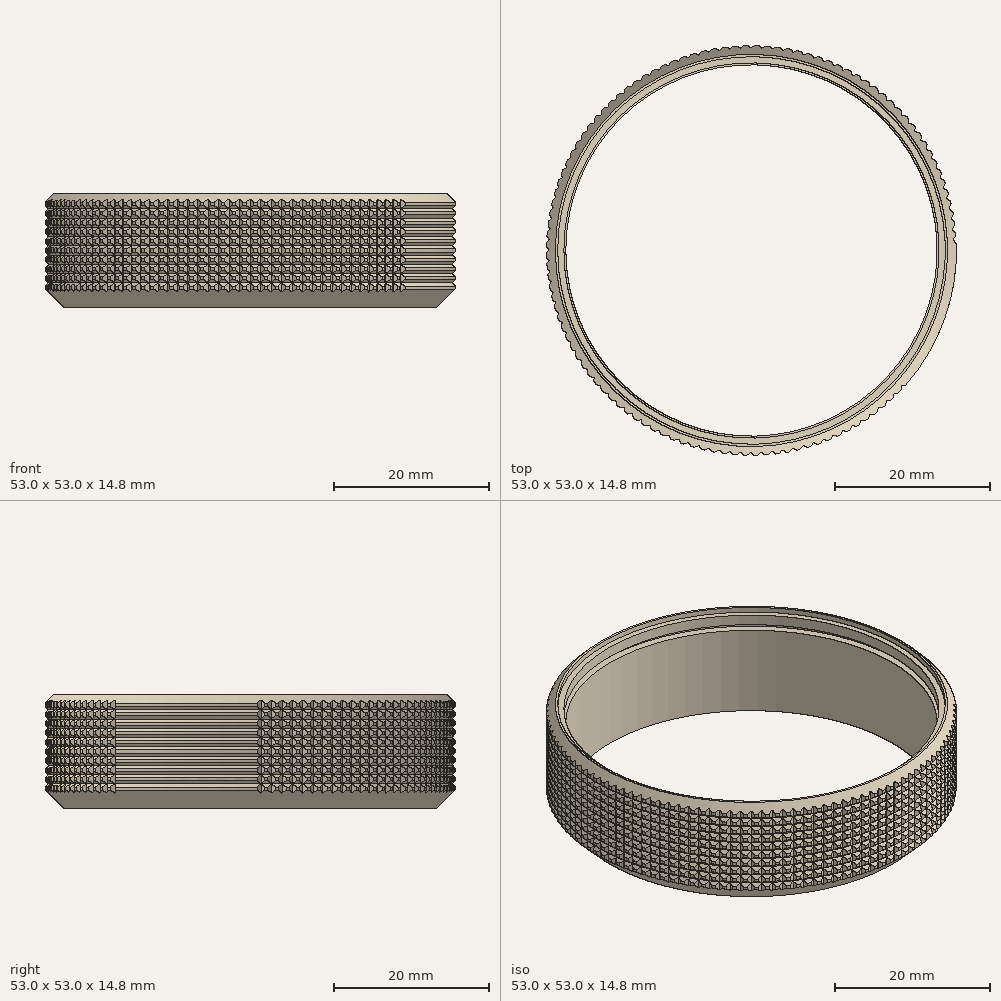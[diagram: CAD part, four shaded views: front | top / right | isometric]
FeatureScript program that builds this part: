
annotation { "Feature Type Name" : "Feature", "Feature Type Description" : "" }
export const myFeature = defineFeature(function(context is Context, id is Id, definition is map)
    precondition{}
    {
        {
            var Q0;
            Q0=qCreatedBy(makeId("Front.planeOp"),FACE);
            var sketch = newSketch(context, id + "F0", { "sketchPlane" : qUnion([Q0])});
            skLineSegment(sketch, "E0", {"start": v(24, 0) * mm, "end": v(24.1, 0) * mm});
            skLineSegment(sketch, "E1", {"start": v(24.1, 0) * mm, "end": v(26.5, 2.4) * mm});
            skLineSegment(sketch, "E2", {"start": v(26.5, 2.4) * mm, "end": v(26.5, 13.65) * mm});
            skLineSegment(sketch, "E3", {"start": v(26.5, 13.65) * mm, "end": v(25.35, 14.8) * mm});
            skLineSegment(sketch, "E4", {"start": v(25.35, 14.8) * mm, "end": v(25.05, 14.8) * mm});
            skLineSegment(sketch, "E5", {"start": v(25.05, 14.8) * mm, "end": v(25.05, 14.1) * mm});
            skLineSegment(sketch, "E6", {"start": v(25.05, 14.1) * mm, "end": v(24.25, 14.1) * mm});
            skLineSegment(sketch, "E7", {"start": v(24.25, 14.1) * mm, "end": v(24.25, 12.7) * mm});
            skLineSegment(sketch, "E8", {"start": v(24.25, 12.7) * mm, "end": v(25.05, 12.7) * mm});
            skLineSegment(sketch, "E9", {"start": v(25.05, 12.7) * mm, "end": v(25.05, 12) * mm});
            skLineSegment(sketch, "E10", {"start": v(25.05, 12) * mm, "end": v(24, 12) * mm});
            skLineSegment(sketch, "E11", {"start": v(24, 12) * mm, "end": v(24, 0) * mm});
            skLineSegment(sketch, "E12", {"start": v(0, 0) * mm, "end": v(0, 14.8) * mm, "construction": true});
            skSolve(sketch);
        }
        {
            var Q0;
            Q0=makeQuery(id+"F0.imprint","IMPRINT",FACE,{"disambiguationData":[TD([[makeQuery(id+"F0.imprint","IMPRINT",EDGE,{"derivedFrom":sQuery(id+"F0.wireOp",EDGE,"E0")}),1.0]])]});
            var Q1;
            Q1=sQuery(id+"F0.wireOp",EDGE,"E12");
            revolve(context, id + "F1", {"entities" : qUnion([Q0]), "axis" : qUnion([Q1]), "revolveType" : RevolveType.FULL});
        }
        {
            var Q0;
            Q0=qCreatedBy(makeId("Front.planeOp"),FACE);
            var sketch = newSketch(context, id + "F2", { "sketchPlane" : qUnion([Q0])});
            skLineSegment(sketch, "E13", {"start": v(26.5, 2.4) * mm, "end": v(26.5, 2.8) * mm});
            skLineSegment(sketch, "E14", {"start": v(26.5, 2.8) * mm, "end": v(26.1, 3.2) * mm});
            skLineSegment(sketch, "E15", {"start": v(26.1, 3.2) * mm, "end": v(26.5, 3.6) * mm});
            skLineSegment(sketch, "E16", {"start": v(26.5, 3.6) * mm, "end": v(26.5, 4) * mm});
            skLineSegment(sketch, "E17", {"start": v(26.5, 4) * mm, "end": v(26.1, 4.4) * mm});
            skLineSegment(sketch, "E18.1.0.0", {"start": v(26.1, 4.4) * mm, "end": v(26.5, 4.8) * mm});
            skLineSegment(sketch, "E18.1.0.1", {"start": v(26.5, 4.8) * mm, "end": v(26.5, 5.2) * mm});
            skLineSegment(sketch, "E18.1.0.2", {"start": v(26.5, 5.2) * mm, "end": v(26.1, 5.6) * mm});
            skLineSegment(sketch, "E18.2.0.0", {"start": v(26.1, 5.6) * mm, "end": v(26.5, 6) * mm});
            skLineSegment(sketch, "E18.2.0.1", {"start": v(26.5, 6) * mm, "end": v(26.5, 6.4) * mm});
            skLineSegment(sketch, "E18.2.0.2", {"start": v(26.5, 6.4) * mm, "end": v(26.1, 6.8) * mm});
            skLineSegment(sketch, "E18.3.0.0", {"start": v(26.1, 6.8) * mm, "end": v(26.5, 7.2) * mm});
            skLineSegment(sketch, "E18.3.0.1", {"start": v(26.5, 7.2) * mm, "end": v(26.5, 7.6) * mm});
            skLineSegment(sketch, "E18.3.0.2", {"start": v(26.5, 7.6) * mm, "end": v(26.1, 8) * mm});
            skLineSegment(sketch, "E18.4.0.0", {"start": v(26.1, 8) * mm, "end": v(26.5, 8.4) * mm});
            skLineSegment(sketch, "E18.4.0.1", {"start": v(26.5, 8.4) * mm, "end": v(26.5, 8.8) * mm});
            skLineSegment(sketch, "E18.4.0.2", {"start": v(26.5, 8.8) * mm, "end": v(26.1, 9.2) * mm});
            skLineSegment(sketch, "E18.5.0.0", {"start": v(26.1, 9.2) * mm, "end": v(26.5, 9.6) * mm});
            skLineSegment(sketch, "E18.5.0.1", {"start": v(26.5, 9.6) * mm, "end": v(26.5, 10) * mm});
            skLineSegment(sketch, "E18.5.0.2", {"start": v(26.5, 10) * mm, "end": v(26.1, 10.4) * mm});
            skLineSegment(sketch, "E18.6.0.0", {"start": v(26.1, 10.4) * mm, "end": v(26.5, 10.8) * mm});
            skLineSegment(sketch, "E18.6.0.1", {"start": v(26.5, 10.8) * mm, "end": v(26.5, 11.2) * mm});
            skLineSegment(sketch, "E18.6.0.2", {"start": v(26.5, 11.2) * mm, "end": v(26.1, 11.6) * mm});
            skLineSegment(sketch, "E18.7.0.0", {"start": v(26.1, 11.6) * mm, "end": v(26.5, 12) * mm});
            skLineSegment(sketch, "E18.7.0.1", {"start": v(26.5, 12) * mm, "end": v(26.5, 12.4) * mm});
            skLineSegment(sketch, "E18.7.0.2", {"start": v(26.5, 12.4) * mm, "end": v(26.1, 12.8) * mm});
            skLineSegment(sketch, "E18.direction1", {"start": v(26.1, 3.2) * mm, "end": v(26.1, 4.4) * mm, "construction": true});
            skLineSegment(sketch, "E19", {"start": v(26.1, 12.8) * mm, "end": v(26.5, 13.2) * mm});
            skLineSegment(sketch, "E20", {"start": v(26.5, 13.2) * mm, "end": v(26.5, 12.4) * mm});
            skLineSegment(sketch, "E21", {"start": v(26.5, 12) * mm, "end": v(26.5, 11.2) * mm});
            skLineSegment(sketch, "E22", {"start": v(26.5, 10.8) * mm, "end": v(26.5, 10) * mm});
            skLineSegment(sketch, "E23", {"start": v(26.5, 9.6) * mm, "end": v(26.5, 8.8) * mm});
            skLineSegment(sketch, "E24", {"start": v(26.5, 8.4) * mm, "end": v(26.5, 7.6) * mm});
            skLineSegment(sketch, "E25", {"start": v(26.5, 7.2) * mm, "end": v(26.5, 6.4) * mm});
            skLineSegment(sketch, "E26", {"start": v(26.5, 6) * mm, "end": v(26.5, 5.2) * mm});
            skLineSegment(sketch, "E27", {"start": v(26.5, 4.8) * mm, "end": v(26.5, 4) * mm});
            skLineSegment(sketch, "E28", {"start": v(26.5, 3.6) * mm, "end": v(26.5, 2.8) * mm});
            skSolve(sketch);
        }
        {
            var Q0;
            {Q0=qUnion([makeQuery(id+"F2.imprint","IMPRINT",FACE,{"disambiguationData":[TD([[makeQuery(id+"F2.imprint","IMPRINT",EDGE,{"derivedFrom":sQuery(id+"F2.wireOp",EDGE,"E14")}),-1.0]])]}),makeQuery(id+"F2.imprint","IMPRINT",FACE,{"disambiguationData":[TD([[makeQuery(id+"F2.imprint","IMPRINT",EDGE,{"derivedFrom":sQuery(id+"F2.wireOp",EDGE,"E17")}),-1.0]])]}),makeQuery(id+"F2.imprint","IMPRINT",FACE,{"disambiguationData":[TD([[makeQuery(id+"F2.imprint","IMPRINT",EDGE,{"derivedFrom":sQuery(id+"F2.wireOp",EDGE,"E18.1.0.2")}),-1.0]])]}),makeQuery(id+"F2.imprint","IMPRINT",FACE,{"disambiguationData":[TD([[makeQuery(id+"F2.imprint","IMPRINT",EDGE,{"derivedFrom":sQuery(id+"F2.wireOp",EDGE,"E18.2.0.2")}),-1.0]])]}),makeQuery(id+"F2.imprint","IMPRINT",FACE,{"disambiguationData":[TD([[makeQuery(id+"F2.imprint","IMPRINT",EDGE,{"derivedFrom":sQuery(id+"F2.wireOp",EDGE,"E18.3.0.2")}),-1.0]])]}),makeQuery(id+"F2.imprint","IMPRINT",FACE,{"disambiguationData":[TD([[makeQuery(id+"F2.imprint","IMPRINT",EDGE,{"derivedFrom":sQuery(id+"F2.wireOp",EDGE,"E18.4.0.2")}),-1.0]])]}),makeQuery(id+"F2.imprint","IMPRINT",FACE,{"disambiguationData":[TD([[makeQuery(id+"F2.imprint","IMPRINT",EDGE,{"derivedFrom":sQuery(id+"F2.wireOp",EDGE,"E18.5.0.2")}),-1.0]])]}),makeQuery(id+"F2.imprint","IMPRINT",FACE,{"disambiguationData":[TD([[makeQuery(id+"F2.imprint","IMPRINT",EDGE,{"derivedFrom":sQuery(id+"F2.wireOp",EDGE,"E18.6.0.2")}),-1.0]])]}),makeQuery(id+"F2.imprint","IMPRINT",FACE,{"disambiguationData":[TD([[makeQuery(id+"F2.imprint","IMPRINT",EDGE,{"derivedFrom":sQuery(id+"F2.wireOp",EDGE,"E18.7.0.2")}),-1.0]])]})]);}
            var Q1;
            Q1=sQuery(id+"F0.wireOp",EDGE,"E12");
            revolve(context, id + "F3", {"operationType" : NewBodyOperationType.REMOVE, "entities" : qUnion([Q0]), "axis" : qUnion([Q1]), "revolveType" : RevolveType.FULL, "oppositeDirection" : true});
        }
        {
            var Q0;
            Q0=qCreatedBy(makeId("Top.planeOp"),FACE);
            var sketch = newSketch(context, id + "F4", { "sketchPlane" : qUnion([Q0])});
            skCircle(sketch, "E29", {"center": v(0, 0) * mm, "radius": 26.5 * mm});
            skCircle(sketch, "E30", {"center": v(0, 0) * mm, "radius": 26.1 * mm});
            skLineSegment(sketch, "E31", {"start": v(26.1, 0) * mm, "end": v(26.5, 0.47) * mm});
            skLineSegment(sketch, "E32", {"start": v(26.49, 0.87) * mm, "end": v(26.06, 1.37) * mm});
            skLineSegment(sketch, "E33", {"start": v(26.06, 1.37) * mm, "end": v(26.46, 1.4) * mm, "construction": true});
            skLineSegment(sketch, "E34.1.0", {"start": v(26.5, -0.52) * mm, "end": v(26.1, 0) * mm});
            skLineSegment(sketch, "E34.1.1", {"start": v(26.48, -0.92) * mm, "end": v(26.5, -0.52) * mm});
            skLineSegment(sketch, "E34.1.2", {"start": v(26.06, -1.37) * mm, "end": v(26.48, -0.92) * mm});
            skLineSegment(sketch, "E34.2.0", {"start": v(26.43, -1.9) * mm, "end": v(26.06, -1.36) * mm});
            skLineSegment(sketch, "E34.2.1", {"start": v(26.4, -2.3) * mm, "end": v(26.43, -1.9) * mm});
            skLineSegment(sketch, "E34.2.2", {"start": v(25.96, -2.73) * mm, "end": v(26.4, -2.3) * mm});
            skLineSegment(sketch, "E34.3.0", {"start": v(26.3, -3.29) * mm, "end": v(25.96, -2.73) * mm});
            skLineSegment(sketch, "E34.3.1", {"start": v(26.24, -3.68) * mm, "end": v(26.3, -3.29) * mm});
            skLineSegment(sketch, "E34.3.2", {"start": v(25.78, -4.09) * mm, "end": v(26.24, -3.68) * mm});
            skLineSegment(sketch, "E34.4.0", {"start": v(26.08, -4.66) * mm, "end": v(25.78, -4.08) * mm});
            skLineSegment(sketch, "E34.4.1", {"start": v(26.01, -5.05) * mm, "end": v(26.08, -4.66) * mm});
            skLineSegment(sketch, "E34.4.2", {"start": v(25.53, -5.43) * mm, "end": v(26.01, -5.05) * mm});
            skLineSegment(sketch, "E34.5.0", {"start": v(25.8, -6.02) * mm, "end": v(25.53, -5.43) * mm});
            skLineSegment(sketch, "E34.5.1", {"start": v(25.71, -6.41) * mm, "end": v(25.8, -6.02) * mm});
            skLineSegment(sketch, "E34.5.2", {"start": v(25.2, -6.76) * mm, "end": v(25.71, -6.41) * mm});
            skLineSegment(sketch, "E34.6.0", {"start": v(25.45, -7.37) * mm, "end": v(25.2, -6.76) * mm});
            skLineSegment(sketch, "E34.6.1", {"start": v(25.34, -7.75) * mm, "end": v(25.45, -7.37) * mm});
            skLineSegment(sketch, "E34.6.2", {"start": v(24.82, -8.08) * mm, "end": v(25.34, -7.75) * mm});
            skLineSegment(sketch, "E34.7.0", {"start": v(25.03, -8.69) * mm, "end": v(24.82, -8.07) * mm});
            skLineSegment(sketch, "E34.7.1", {"start": v(24.9, -9.07) * mm, "end": v(25.03, -8.69) * mm});
            skLineSegment(sketch, "E34.7.2", {"start": v(24.36, -9.37) * mm, "end": v(24.9, -9.07) * mm});
            skLineSegment(sketch, "E34.8.0", {"start": v(24.54, -9.99) * mm, "end": v(24.36, -9.36) * mm});
            skLineSegment(sketch, "E34.8.1", {"start": v(24.39, -10.36) * mm, "end": v(24.54, -9.99) * mm});
            skLineSegment(sketch, "E34.8.2", {"start": v(23.84, -10.63) * mm, "end": v(24.39, -10.36) * mm});
            skLineSegment(sketch, "E34.9.0", {"start": v(23.99, -11.26) * mm, "end": v(23.84, -10.62) * mm});
            skLineSegment(sketch, "E34.9.1", {"start": v(23.81, -11.62) * mm, "end": v(23.99, -11.26) * mm});
            skLineSegment(sketch, "E34.9.2", {"start": v(23.25, -11.86) * mm, "end": v(23.81, -11.62) * mm});
            skLineSegment(sketch, "E34.10.0", {"start": v(23.36, -12.5) * mm, "end": v(23.25, -11.86) * mm});
            skLineSegment(sketch, "E34.10.1", {"start": v(23.17, -12.86) * mm, "end": v(23.36, -12.5) * mm});
            skLineSegment(sketch, "E34.10.2", {"start": v(22.6, -13.07) * mm, "end": v(23.17, -12.86) * mm});
            skLineSegment(sketch, "E34.11.0", {"start": v(22.67, -13.71) * mm, "end": v(22.6, -13.06) * mm});
            skLineSegment(sketch, "E34.11.1", {"start": v(22.47, -14.05) * mm, "end": v(22.67, -13.71) * mm});
            skLineSegment(sketch, "E34.11.2", {"start": v(21.88, -14.23) * mm, "end": v(22.47, -14.05) * mm});
            skLineSegment(sketch, "E34.12.0", {"start": v(21.93, -14.88) * mm, "end": v(21.88, -14.23) * mm});
            skLineSegment(sketch, "E34.12.1", {"start": v(21.7, -15.21) * mm, "end": v(21.93, -14.88) * mm});
            skLineSegment(sketch, "E34.12.2", {"start": v(21.1, -15.36) * mm, "end": v(21.7, -15.21) * mm});
            skLineSegment(sketch, "E34.13.0", {"start": v(21.12, -16) * mm, "end": v(21.1, -15.35) * mm});
            skLineSegment(sketch, "E34.13.1", {"start": v(20.87, -16.33) * mm, "end": v(21.12, -16) * mm});
            skLineSegment(sketch, "E34.13.2", {"start": v(20.27, -16.44) * mm, "end": v(20.87, -16.33) * mm});
            skLineSegment(sketch, "E34.14.0", {"start": v(20.25, -17.1) * mm, "end": v(20.27, -16.44) * mm});
            skLineSegment(sketch, "E34.14.1", {"start": v(19.99, -17.4) * mm, "end": v(20.25, -17.1) * mm});
            skLineSegment(sketch, "E34.14.2", {"start": v(19.38, -17.48) * mm, "end": v(19.99, -17.4) * mm});
            skLineSegment(sketch, "E34.15.0", {"start": v(19.33, -18.13) * mm, "end": v(19.38, -17.48) * mm});
            skLineSegment(sketch, "E34.15.1", {"start": v(19.05, -18.42) * mm, "end": v(19.33, -18.13) * mm});
            skLineSegment(sketch, "E34.15.2", {"start": v(18.44, -18.48) * mm, "end": v(19.05, -18.42) * mm});
            skLineSegment(sketch, "E34.16.0", {"start": v(18.35, -19.12) * mm, "end": v(18.44, -18.47) * mm});
            skLineSegment(sketch, "E34.16.1", {"start": v(18.06, -19.4) * mm, "end": v(18.35, -19.12) * mm});
            skLineSegment(sketch, "E34.16.2", {"start": v(17.44, -19.42) * mm, "end": v(18.06, -19.4) * mm});
            skLineSegment(sketch, "E34.17.0", {"start": v(17.32, -20.06) * mm, "end": v(17.45, -19.41) * mm});
            skLineSegment(sketch, "E34.17.1", {"start": v(17.02, -20.32) * mm, "end": v(17.32, -20.06) * mm});
            skLineSegment(sketch, "E34.17.2", {"start": v(16.4, -20.3) * mm, "end": v(17.02, -20.32) * mm});
            skLineSegment(sketch, "E34.18.0", {"start": v(16.25, -20.94) * mm, "end": v(16.4, -20.3) * mm});
            skLineSegment(sketch, "E34.18.1", {"start": v(15.93, -21.18) * mm, "end": v(16.25, -20.94) * mm});
            skLineSegment(sketch, "E34.18.2", {"start": v(15.32, -21.14) * mm, "end": v(15.93, -21.18) * mm});
            skLineSegment(sketch, "E34.19.0", {"start": v(15.13, -21.76) * mm, "end": v(15.32, -21.13) * mm});
            skLineSegment(sketch, "E34.19.1", {"start": v(14.8, -21.99) * mm, "end": v(15.13, -21.76) * mm});
            skLineSegment(sketch, "E34.19.2", {"start": v(14.19, -21.91) * mm, "end": v(14.8, -21.99) * mm});
            skLineSegment(sketch, "E34.20.0", {"start": v(13.97, -22.53) * mm, "end": v(14.2, -21.9) * mm});
            skLineSegment(sketch, "E34.20.1", {"start": v(13.63, -22.73) * mm, "end": v(13.97, -22.53) * mm});
            skLineSegment(sketch, "E34.20.2", {"start": v(13.02, -22.63) * mm, "end": v(13.63, -22.73) * mm});
            skLineSegment(sketch, "E34.21.0", {"start": v(12.77, -23.23) * mm, "end": v(13.03, -22.62) * mm});
            skLineSegment(sketch, "E34.21.1", {"start": v(12.42, -23.42) * mm, "end": v(12.77, -23.23) * mm});
            skLineSegment(sketch, "E34.21.2", {"start": v(11.82, -23.28) * mm, "end": v(12.42, -23.42) * mm});
            skLineSegment(sketch, "E34.22.0", {"start": v(11.54, -23.87) * mm, "end": v(11.82, -23.28) * mm});
            skLineSegment(sketch, "E34.22.1", {"start": v(11.18, -24.04) * mm, "end": v(11.54, -23.87) * mm});
            skLineSegment(sketch, "E34.22.2", {"start": v(10.58, -23.87) * mm, "end": v(11.18, -24.04) * mm});
            skLineSegment(sketch, "E34.23.0", {"start": v(10.27, -24.44) * mm, "end": v(10.59, -23.86) * mm});
            skLineSegment(sketch, "E34.23.1", {"start": v(9.9, -24.6) * mm, "end": v(10.27, -24.44) * mm});
            skLineSegment(sketch, "E34.23.2", {"start": v(9.32, -24.4) * mm, "end": v(9.9, -24.6) * mm});
            skLineSegment(sketch, "E34.24.0", {"start": v(8.98, -24.94) * mm, "end": v(9.33, -24.39) * mm});
            skLineSegment(sketch, "E34.24.1", {"start": v(8.6, -25.08) * mm, "end": v(8.98, -24.94) * mm});
            skLineSegment(sketch, "E34.24.2", {"start": v(8.03, -24.85) * mm, "end": v(8.6, -25.08) * mm});
            skLineSegment(sketch, "E34.25.0", {"start": v(7.66, -25.38) * mm, "end": v(8.04, -24.84) * mm});
            skLineSegment(sketch, "E34.25.1", {"start": v(7.27, -25.5) * mm, "end": v(7.66, -25.38) * mm});
            skLineSegment(sketch, "E34.25.2", {"start": v(6.72, -25.24) * mm, "end": v(7.27, -25.5) * mm});
            skLineSegment(sketch, "E34.26.0", {"start": v(6.32, -25.75) * mm, "end": v(6.72, -25.23) * mm});
            skLineSegment(sketch, "E34.26.1", {"start": v(5.93, -25.84) * mm, "end": v(6.32, -25.75) * mm});
            skLineSegment(sketch, "E34.26.2", {"start": v(5.39, -25.55) * mm, "end": v(5.93, -25.84) * mm});
            skLineSegment(sketch, "E34.27.0", {"start": v(4.96, -26.05) * mm, "end": v(5.4, -25.55) * mm});
            skLineSegment(sketch, "E34.27.1", {"start": v(4.57, -26.12) * mm, "end": v(4.96, -26.05) * mm});
            skLineSegment(sketch, "E34.27.2", {"start": v(4.04, -25.8) * mm, "end": v(4.57, -26.12) * mm});
            skLineSegment(sketch, "E34.28.0", {"start": v(3.6, -26.27) * mm, "end": v(4.05, -25.8) * mm});
            skLineSegment(sketch, "E34.28.1", {"start": v(3.2, -26.33) * mm, "end": v(3.6, -26.27) * mm});
            skLineSegment(sketch, "E34.28.2", {"start": v(2.68, -25.98) * mm, "end": v(3.2, -26.33) * mm});
            skLineSegment(sketch, "E34.29.0", {"start": v(2.21, -26.43) * mm, "end": v(2.7, -25.98) * mm});
            skLineSegment(sketch, "E34.29.1", {"start": v(1.81, -26.46) * mm, "end": v(2.21, -26.43) * mm});
            skLineSegment(sketch, "E34.29.2", {"start": v(1.32, -26.09) * mm, "end": v(1.81, -26.46) * mm});
            skLineSegment(sketch, "E34.30.0", {"start": v(0.82, -26.5) * mm, "end": v(1.33, -26.09) * mm});
            skLineSegment(sketch, "E34.30.1", {"start": v(0.42, -26.52) * mm, "end": v(0.82, -26.5) * mm});
            skLineSegment(sketch, "E34.30.2", {"start": v(-0.05, -26.12) * mm, "end": v(0.42, -26.52) * mm});
            skLineSegment(sketch, "E34.31.0", {"start": v(-0.57, -26.52) * mm, "end": v(-0.04, -26.12) * mm});
            skLineSegment(sketch, "E34.31.1", {"start": v(-0.97, -26.5) * mm, "end": v(-0.57, -26.52) * mm});
            skLineSegment(sketch, "E34.31.2", {"start": v(-1.42, -26.09) * mm, "end": v(-0.97, -26.5) * mm});
            skLineSegment(sketch, "E34.32.0", {"start": v(-1.95, -26.45) * mm, "end": v(-1.4, -26.09) * mm});
            skLineSegment(sketch, "E34.32.1", {"start": v(-2.35, -26.42) * mm, "end": v(-1.95, -26.45) * mm});
            skLineSegment(sketch, "E34.32.2", {"start": v(-2.78, -25.98) * mm, "end": v(-2.35, -26.42) * mm});
            skLineSegment(sketch, "E34.33.0", {"start": v(-3.34, -26.32) * mm, "end": v(-2.77, -25.98) * mm});
            skLineSegment(sketch, "E34.33.1", {"start": v(-3.73, -26.26) * mm, "end": v(-3.34, -26.32) * mm});
            skLineSegment(sketch, "E34.33.2", {"start": v(-4.14, -25.8) * mm, "end": v(-3.73, -26.26) * mm});
            skLineSegment(sketch, "E34.34.0", {"start": v(-4.7, -26.1) * mm, "end": v(-4.13, -25.8) * mm});
            skLineSegment(sketch, "E34.34.1", {"start": v(-5.1, -26.03) * mm, "end": v(-4.7, -26.1) * mm});
            skLineSegment(sketch, "E34.34.2", {"start": v(-5.48, -25.55) * mm, "end": v(-5.1, -26.03) * mm});
            skLineSegment(sketch, "E34.35.0", {"start": v(-6.07, -25.83) * mm, "end": v(-5.47, -25.55) * mm});
            skLineSegment(sketch, "E34.35.1", {"start": v(-6.46, -25.73) * mm, "end": v(-6.07, -25.83) * mm});
            skLineSegment(sketch, "E34.35.2", {"start": v(-6.81, -25.23) * mm, "end": v(-6.46, -25.73) * mm});
            skLineSegment(sketch, "E34.36.0", {"start": v(-7.41, -25.48) * mm, "end": v(-6.8, -25.23) * mm});
            skLineSegment(sketch, "E34.36.1", {"start": v(-7.8, -25.36) * mm, "end": v(-7.41, -25.48) * mm});
            skLineSegment(sketch, "E34.36.2", {"start": v(-8.12, -24.84) * mm, "end": v(-7.8, -25.36) * mm});
            skLineSegment(sketch, "E34.37.0", {"start": v(-8.74, -25.05) * mm, "end": v(-8.12, -24.84) * mm});
            skLineSegment(sketch, "E34.37.1", {"start": v(-9.11, -24.92) * mm, "end": v(-8.74, -25.05) * mm});
            skLineSegment(sketch, "E34.37.2", {"start": v(-9.41, -24.38) * mm, "end": v(-9.11, -24.92) * mm});
            skLineSegment(sketch, "E34.38.0", {"start": v(-10.04, -24.56) * mm, "end": v(-9.4, -24.38) * mm});
            skLineSegment(sketch, "E34.38.1", {"start": v(-10.4, -24.41) * mm, "end": v(-10.04, -24.56) * mm});
            skLineSegment(sketch, "E34.38.2", {"start": v(-10.68, -23.86) * mm, "end": v(-10.4, -24.41) * mm});
            skLineSegment(sketch, "E34.39.0", {"start": v(-11.3, -24) * mm, "end": v(-10.67, -23.86) * mm});
            skLineSegment(sketch, "E34.39.1", {"start": v(-11.67, -23.84) * mm, "end": v(-11.3, -24) * mm});
            skLineSegment(sketch, "E34.39.2", {"start": v(-11.91, -23.27) * mm, "end": v(-11.67, -23.84) * mm});
            skLineSegment(sketch, "E34.40.0", {"start": v(-12.55, -23.38) * mm, "end": v(-11.9, -23.27) * mm});
            skLineSegment(sketch, "E34.40.1", {"start": v(-12.9, -23.2) * mm, "end": v(-12.55, -23.38) * mm});
            skLineSegment(sketch, "E34.40.2", {"start": v(-13.11, -22.61) * mm, "end": v(-12.9, -23.2) * mm});
            skLineSegment(sketch, "E34.41.0", {"start": v(-13.76, -22.7) * mm, "end": v(-13.1, -22.62) * mm});
            skLineSegment(sketch, "E34.41.1", {"start": v(-14.1, -22.49) * mm, "end": v(-13.76, -22.7) * mm});
            skLineSegment(sketch, "E34.41.2", {"start": v(-14.28, -21.9) * mm, "end": v(-14.1, -22.49) * mm});
            skLineSegment(sketch, "E34.42.0", {"start": v(-14.93, -21.95) * mm, "end": v(-14.27, -21.9) * mm});
            skLineSegment(sketch, "E34.42.1", {"start": v(-15.26, -21.72) * mm, "end": v(-14.93, -21.95) * mm});
            skLineSegment(sketch, "E34.42.2", {"start": v(-15.4, -21.12) * mm, "end": v(-15.26, -21.72) * mm});
            skLineSegment(sketch, "E34.43.0", {"start": v(-16.06, -21.14) * mm, "end": v(-15.4, -21.13) * mm});
            skLineSegment(sketch, "E34.43.1", {"start": v(-16.37, -20.9) * mm, "end": v(-16.06, -21.14) * mm});
            skLineSegment(sketch, "E34.43.2", {"start": v(-16.5, -20.3) * mm, "end": v(-16.37, -20.9) * mm});
            skLineSegment(sketch, "E34.44.0", {"start": v(-17.14, -20.27) * mm, "end": v(-16.49, -20.3) * mm});
            skLineSegment(sketch, "E34.44.1", {"start": v(-17.45, -20.01) * mm, "end": v(-17.14, -20.27) * mm});
            skLineSegment(sketch, "E34.44.2", {"start": v(-17.53, -19.4) * mm, "end": v(-17.45, -20.01) * mm});
            skLineSegment(sketch, "E34.45.0", {"start": v(-18.18, -19.35) * mm, "end": v(-17.53, -19.4) * mm});
            skLineSegment(sketch, "E34.45.1", {"start": v(-18.47, -19.07) * mm, "end": v(-18.18, -19.35) * mm});
            skLineSegment(sketch, "E34.45.2", {"start": v(-18.52, -18.46) * mm, "end": v(-18.47, -19.07) * mm});
            skLineSegment(sketch, "E34.46.0", {"start": v(-19.17, -18.37) * mm, "end": v(-18.52, -18.46) * mm});
            skLineSegment(sketch, "E34.46.1", {"start": v(-19.44, -18.08) * mm, "end": v(-19.17, -18.37) * mm});
            skLineSegment(sketch, "E34.46.2", {"start": v(-19.47, -17.47) * mm, "end": v(-19.44, -18.08) * mm});
            skLineSegment(sketch, "E34.47.0", {"start": v(-20.1, -17.35) * mm, "end": v(-19.46, -17.47) * mm});
            skLineSegment(sketch, "E34.47.1", {"start": v(-20.36, -17.04) * mm, "end": v(-20.1, -17.35) * mm});
            skLineSegment(sketch, "E34.47.2", {"start": v(-20.35, -16.42) * mm, "end": v(-20.36, -17.04) * mm});
            skLineSegment(sketch, "E34.48.0", {"start": v(-20.99, -16.27) * mm, "end": v(-20.35, -16.43) * mm});
            skLineSegment(sketch, "E34.48.1", {"start": v(-21.23, -15.95) * mm, "end": v(-20.99, -16.27) * mm});
            skLineSegment(sketch, "E34.48.2", {"start": v(-21.19, -15.34) * mm, "end": v(-21.23, -15.95) * mm});
            skLineSegment(sketch, "E34.49.0", {"start": v(-21.8, -15.15) * mm, "end": v(-21.18, -15.34) * mm});
            skLineSegment(sketch, "E34.49.1", {"start": v(-22.04, -14.82) * mm, "end": v(-21.8, -15.15) * mm});
            skLineSegment(sketch, "E34.49.2", {"start": v(-21.96, -14.21) * mm, "end": v(-22.04, -14.82) * mm});
            skLineSegment(sketch, "E34.50.0", {"start": v(-22.57, -14) * mm, "end": v(-21.96, -14.22) * mm});
            skLineSegment(sketch, "E34.50.1", {"start": v(-22.78, -13.65) * mm, "end": v(-22.57, -14) * mm});
            skLineSegment(sketch, "E34.50.2", {"start": v(-22.68, -13.04) * mm, "end": v(-22.78, -13.65) * mm});
            skLineSegment(sketch, "E34.51.0", {"start": v(-23.28, -12.8) * mm, "end": v(-22.67, -13.05) * mm});
            skLineSegment(sketch, "E34.51.1", {"start": v(-23.47, -12.44) * mm, "end": v(-23.28, -12.8) * mm});
            skLineSegment(sketch, "E34.51.2", {"start": v(-23.33, -11.84) * mm, "end": v(-23.47, -12.44) * mm});
            skLineSegment(sketch, "E34.52.0", {"start": v(-23.91, -11.56) * mm, "end": v(-23.32, -11.85) * mm});
            skLineSegment(sketch, "E34.52.1", {"start": v(-24.09, -11.2) * mm, "end": v(-23.91, -11.56) * mm});
            skLineSegment(sketch, "E34.52.2", {"start": v(-23.92, -10.6) * mm, "end": v(-24.09, -11.2) * mm});
            skLineSegment(sketch, "E34.53.0", {"start": v(-24.49, -10.3) * mm, "end": v(-23.91, -10.61) * mm});
            skLineSegment(sketch, "E34.53.1", {"start": v(-24.64, -9.92) * mm, "end": v(-24.49, -10.3) * mm});
            skLineSegment(sketch, "E34.53.2", {"start": v(-24.44, -9.34) * mm, "end": v(-24.64, -9.92) * mm});
            skLineSegment(sketch, "E34.54.0", {"start": v(-25, -9) * mm, "end": v(-24.44, -9.35) * mm});
            skLineSegment(sketch, "E34.54.1", {"start": v(-25.13, -8.62) * mm, "end": v(-25, -9) * mm});
            skLineSegment(sketch, "E34.54.2", {"start": v(-24.9, -8.05) * mm, "end": v(-25.13, -8.62) * mm});
            skLineSegment(sketch, "E34.55.0", {"start": v(-25.43, -7.68) * mm, "end": v(-24.9, -8.06) * mm});
            skLineSegment(sketch, "E34.55.1", {"start": v(-25.54, -7.3) * mm, "end": v(-25.43, -7.68) * mm});
            skLineSegment(sketch, "E34.55.2", {"start": v(-25.28, -6.74) * mm, "end": v(-25.54, -7.3) * mm});
            skLineSegment(sketch, "E34.56.0", {"start": v(-25.8, -6.34) * mm, "end": v(-25.28, -6.75) * mm});
            skLineSegment(sketch, "E34.56.1", {"start": v(-25.9, -5.95) * mm, "end": v(-25.8, -6.34) * mm});
            skLineSegment(sketch, "E34.56.2", {"start": v(-25.6, -5.4) * mm, "end": v(-25.9, -5.95) * mm});
            skLineSegment(sketch, "E34.57.0", {"start": v(-26.1, -4.98) * mm, "end": v(-25.6, -5.42) * mm});
            skLineSegment(sketch, "E34.57.1", {"start": v(-26.17, -4.6) * mm, "end": v(-26.1, -4.98) * mm});
            skLineSegment(sketch, "E34.57.2", {"start": v(-25.85, -4.06) * mm, "end": v(-26.17, -4.6) * mm});
            skLineSegment(sketch, "E34.58.0", {"start": v(-26.32, -3.61) * mm, "end": v(-25.85, -4.07) * mm});
            skLineSegment(sketch, "E34.58.1", {"start": v(-26.37, -3.22) * mm, "end": v(-26.32, -3.61) * mm});
            skLineSegment(sketch, "E34.58.2", {"start": v(-26.03, -2.7) * mm, "end": v(-26.37, -3.22) * mm});
            skLineSegment(sketch, "E34.59.0", {"start": v(-26.47, -2.23) * mm, "end": v(-26.03, -2.71) * mm});
            skLineSegment(sketch, "E34.59.1", {"start": v(-26.5, -1.83) * mm, "end": v(-26.47, -2.23) * mm});
            skLineSegment(sketch, "E34.59.2", {"start": v(-26.14, -1.34) * mm, "end": v(-26.5, -1.83) * mm});
            skLineSegment(sketch, "E34.60.0", {"start": v(-26.56, -0.85) * mm, "end": v(-26.13, -1.35) * mm});
            skLineSegment(sketch, "E34.60.1", {"start": v(-26.57, -0.45) * mm, "end": v(-26.56, -0.85) * mm});
            skLineSegment(sketch, "E34.60.2", {"start": v(-26.17, 0.03) * mm, "end": v(-26.57, -0.45) * mm});
            skLineSegment(sketch, "E34.61.0", {"start": v(-26.56, 0.54) * mm, "end": v(-26.17, 0.02) * mm});
            skLineSegment(sketch, "E34.61.1", {"start": v(-26.55, 0.94) * mm, "end": v(-26.56, 0.54) * mm});
            skLineSegment(sketch, "E34.61.2", {"start": v(-26.13, 1.4) * mm, "end": v(-26.55, 0.94) * mm});
            skLineSegment(sketch, "E34.62.0", {"start": v(-26.5, 1.93) * mm, "end": v(-26.13, 1.39) * mm});
            skLineSegment(sketch, "E34.62.1", {"start": v(-26.47, 2.33) * mm, "end": v(-26.5, 1.93) * mm});
            skLineSegment(sketch, "E34.62.2", {"start": v(-26.03, 2.76) * mm, "end": v(-26.47, 2.33) * mm});
            skLineSegment(sketch, "E34.63.0", {"start": v(-26.36, 3.31) * mm, "end": v(-26.03, 2.75) * mm});
            skLineSegment(sketch, "E34.63.1", {"start": v(-26.31, 3.7) * mm, "end": v(-26.36, 3.31) * mm});
            skLineSegment(sketch, "E34.63.2", {"start": v(-25.85, 4.11) * mm, "end": v(-26.31, 3.7) * mm});
            skLineSegment(sketch, "E34.64.0", {"start": v(-26.16, 4.69) * mm, "end": v(-25.85, 4.1) * mm});
            skLineSegment(sketch, "E34.64.1", {"start": v(-26.08, 5.08) * mm, "end": v(-26.16, 4.69) * mm});
            skLineSegment(sketch, "E34.64.2", {"start": v(-25.6, 5.46) * mm, "end": v(-26.08, 5.08) * mm});
            skLineSegment(sketch, "E34.65.0", {"start": v(-25.87, 6.05) * mm, "end": v(-25.6, 5.45) * mm});
            skLineSegment(sketch, "E34.65.1", {"start": v(-25.78, 6.44) * mm, "end": v(-25.87, 6.05) * mm});
            skLineSegment(sketch, "E34.65.2", {"start": v(-25.28, 6.79) * mm, "end": v(-25.78, 6.44) * mm});
            skLineSegment(sketch, "E34.66.0", {"start": v(-25.52, 7.4) * mm, "end": v(-25.28, 6.78) * mm});
            skLineSegment(sketch, "E34.66.1", {"start": v(-25.4, 7.77) * mm, "end": v(-25.52, 7.4) * mm});
            skLineSegment(sketch, "E34.66.2", {"start": v(-24.89, 8.1) * mm, "end": v(-25.4, 7.77) * mm});
            skLineSegment(sketch, "E34.67.0", {"start": v(-25.1, 8.71) * mm, "end": v(-24.89, 8.1) * mm});
            skLineSegment(sketch, "E34.67.1", {"start": v(-24.97, 9.1) * mm, "end": v(-25.1, 8.71) * mm});
            skLineSegment(sketch, "E34.67.2", {"start": v(-24.43, 9.4) * mm, "end": v(-24.97, 9.1) * mm});
            skLineSegment(sketch, "E34.68.0", {"start": v(-24.61, 10.01) * mm, "end": v(-24.43, 9.38) * mm});
            skLineSegment(sketch, "E34.68.1", {"start": v(-24.46, 10.38) * mm, "end": v(-24.61, 10.01) * mm});
            skLineSegment(sketch, "E34.68.2", {"start": v(-23.9, 10.65) * mm, "end": v(-24.46, 10.38) * mm});
            skLineSegment(sketch, "E34.69.0", {"start": v(-24.06, 11.29) * mm, "end": v(-23.9, 10.65) * mm});
            skLineSegment(sketch, "E34.69.1", {"start": v(-23.88, 11.65) * mm, "end": v(-24.06, 11.29) * mm});
            skLineSegment(sketch, "E34.69.2", {"start": v(-23.32, 11.89) * mm, "end": v(-23.88, 11.65) * mm});
            skLineSegment(sketch, "E34.70.0", {"start": v(-23.43, 12.53) * mm, "end": v(-23.32, 11.88) * mm});
            skLineSegment(sketch, "E34.70.1", {"start": v(-23.24, 12.88) * mm, "end": v(-23.43, 12.53) * mm});
            skLineSegment(sketch, "E34.70.2", {"start": v(-22.66, 13.1) * mm, "end": v(-23.24, 12.88) * mm});
            skLineSegment(sketch, "E34.71.0", {"start": v(-22.75, 13.74) * mm, "end": v(-22.67, 13.08) * mm});
            skLineSegment(sketch, "E34.71.1", {"start": v(-22.54, 14.08) * mm, "end": v(-22.75, 13.74) * mm});
            skLineSegment(sketch, "E34.71.2", {"start": v(-21.95, 14.26) * mm, "end": v(-22.54, 14.08) * mm});
            skLineSegment(sketch, "E34.72.0", {"start": v(-22, 14.9) * mm, "end": v(-21.95, 14.25) * mm});
            skLineSegment(sketch, "E34.72.1", {"start": v(-21.77, 15.24) * mm, "end": v(-22, 14.9) * mm});
            skLineSegment(sketch, "E34.72.2", {"start": v(-21.17, 15.38) * mm, "end": v(-21.77, 15.24) * mm});
            skLineSegment(sketch, "E34.73.0", {"start": v(-21.19, 16.04) * mm, "end": v(-21.17, 15.38) * mm});
            skLineSegment(sketch, "E34.73.1", {"start": v(-20.94, 16.35) * mm, "end": v(-21.19, 16.04) * mm});
            skLineSegment(sketch, "E34.73.2", {"start": v(-20.34, 16.47) * mm, "end": v(-20.94, 16.35) * mm});
            skLineSegment(sketch, "E34.74.0", {"start": v(-20.32, 17.12) * mm, "end": v(-20.34, 16.46) * mm});
            skLineSegment(sketch, "E34.74.1", {"start": v(-20.06, 17.42) * mm, "end": v(-20.32, 17.12) * mm});
            skLineSegment(sketch, "E34.74.2", {"start": v(-19.45, 17.5) * mm, "end": v(-20.06, 17.42) * mm});
            skLineSegment(sketch, "E34.75.0", {"start": v(-19.4, 18.16) * mm, "end": v(-19.45, 17.5) * mm});
            skLineSegment(sketch, "E34.75.1", {"start": v(-19.12, 18.45) * mm, "end": v(-19.4, 18.16) * mm});
            skLineSegment(sketch, "E34.75.2", {"start": v(-18.5, 18.5) * mm, "end": v(-19.12, 18.45) * mm});
            skLineSegment(sketch, "E34.76.0", {"start": v(-18.42, 19.15) * mm, "end": v(-18.51, 18.5) * mm});
            skLineSegment(sketch, "E34.76.1", {"start": v(-18.13, 19.42) * mm, "end": v(-18.42, 19.15) * mm});
            skLineSegment(sketch, "E34.76.2", {"start": v(-17.51, 19.44) * mm, "end": v(-18.13, 19.42) * mm});
            skLineSegment(sketch, "E34.77.0", {"start": v(-17.4, 20.08) * mm, "end": v(-17.52, 19.44) * mm});
            skLineSegment(sketch, "E34.77.1", {"start": v(-17.09, 20.34) * mm, "end": v(-17.4, 20.08) * mm});
            skLineSegment(sketch, "E34.77.2", {"start": v(-16.47, 20.33) * mm, "end": v(-17.09, 20.34) * mm});
            skLineSegment(sketch, "E34.78.0", {"start": v(-16.32, 20.96) * mm, "end": v(-16.48, 20.33) * mm});
            skLineSegment(sketch, "E34.78.1", {"start": v(-16, 21.2) * mm, "end": v(-16.32, 20.96) * mm});
            skLineSegment(sketch, "E34.78.2", {"start": v(-15.39, 21.16) * mm, "end": v(-16, 21.2) * mm});
            skLineSegment(sketch, "E34.79.0", {"start": v(-15.2, 21.79) * mm, "end": v(-15.4, 21.16) * mm});
            skLineSegment(sketch, "E34.79.1", {"start": v(-14.87, 22.01) * mm, "end": v(-15.2, 21.79) * mm});
            skLineSegment(sketch, "E34.79.2", {"start": v(-14.26, 21.94) * mm, "end": v(-14.87, 22.01) * mm});
            skLineSegment(sketch, "E34.80.0", {"start": v(-14.04, 22.55) * mm, "end": v(-14.26, 21.93) * mm});
            skLineSegment(sketch, "E34.80.1", {"start": v(-13.7, 22.76) * mm, "end": v(-14.04, 22.55) * mm});
            skLineSegment(sketch, "E34.80.2", {"start": v(-13.1, 22.65) * mm, "end": v(-13.7, 22.76) * mm});
            skLineSegment(sketch, "E34.81.0", {"start": v(-12.84, 23.25) * mm, "end": v(-13.1, 22.65) * mm});
            skLineSegment(sketch, "E34.81.1", {"start": v(-12.49, 23.44) * mm, "end": v(-12.84, 23.25) * mm});
            skLineSegment(sketch, "E34.81.2", {"start": v(-11.89, 23.3) * mm, "end": v(-12.49, 23.44) * mm});
            skLineSegment(sketch, "E34.82.0", {"start": v(-11.6, 23.9) * mm, "end": v(-11.9, 23.3) * mm});
            skLineSegment(sketch, "E34.82.1", {"start": v(-11.25, 24.06) * mm, "end": v(-11.6, 23.9) * mm});
            skLineSegment(sketch, "E34.82.2", {"start": v(-10.65, 23.9) * mm, "end": v(-11.25, 24.06) * mm});
            skLineSegment(sketch, "E34.83.0", {"start": v(-10.34, 24.46) * mm, "end": v(-10.66, 23.9) * mm});
            skLineSegment(sketch, "E34.83.1", {"start": v(-9.97, 24.62) * mm, "end": v(-10.34, 24.46) * mm});
            skLineSegment(sketch, "E34.83.2", {"start": v(-9.39, 24.42) * mm, "end": v(-9.97, 24.62) * mm});
            skLineSegment(sketch, "E34.84.0", {"start": v(-9.05, 24.97) * mm, "end": v(-9.4, 24.41) * mm});
            skLineSegment(sketch, "E34.84.1", {"start": v(-8.67, 25.1) * mm, "end": v(-9.05, 24.97) * mm});
            skLineSegment(sketch, "E34.84.2", {"start": v(-8.1, 24.87) * mm, "end": v(-8.67, 25.1) * mm});
            skLineSegment(sketch, "E34.85.0", {"start": v(-7.73, 25.4) * mm, "end": v(-8.1, 24.87) * mm});
            skLineSegment(sketch, "E34.85.1", {"start": v(-7.35, 25.52) * mm, "end": v(-7.73, 25.4) * mm});
            skLineSegment(sketch, "E34.85.2", {"start": v(-6.79, 25.26) * mm, "end": v(-7.35, 25.52) * mm});
            skLineSegment(sketch, "E34.86.0", {"start": v(-6.39, 25.78) * mm, "end": v(-6.8, 25.26) * mm});
            skLineSegment(sketch, "E34.86.1", {"start": v(-6, 25.87) * mm, "end": v(-6.39, 25.78) * mm});
            skLineSegment(sketch, "E34.86.2", {"start": v(-5.46, 25.58) * mm, "end": v(-6, 25.87) * mm});
            skLineSegment(sketch, "E34.87.0", {"start": v(-5.03, 26.07) * mm, "end": v(-5.46, 25.58) * mm});
            skLineSegment(sketch, "E34.87.1", {"start": v(-4.64, 26.15) * mm, "end": v(-5.03, 26.07) * mm});
            skLineSegment(sketch, "E34.87.2", {"start": v(-4.11, 25.83) * mm, "end": v(-4.64, 26.15) * mm});
            skLineSegment(sketch, "E34.88.0", {"start": v(-3.66, 26.3) * mm, "end": v(-4.12, 25.83) * mm});
            skLineSegment(sketch, "E34.88.1", {"start": v(-3.26, 26.35) * mm, "end": v(-3.66, 26.3) * mm});
            skLineSegment(sketch, "E34.88.2", {"start": v(-2.75, 26) * mm, "end": v(-3.26, 26.35) * mm});
            skLineSegment(sketch, "E34.89.0", {"start": v(-2.28, 26.45) * mm, "end": v(-2.76, 26) * mm});
            skLineSegment(sketch, "E34.89.1", {"start": v(-1.88, 26.48) * mm, "end": v(-2.28, 26.45) * mm});
            skLineSegment(sketch, "E34.89.2", {"start": v(-1.4, 26.11) * mm, "end": v(-1.88, 26.48) * mm});
            skLineSegment(sketch, "E34.90.0", {"start": v(-0.9, 26.53) * mm, "end": v(-1.4, 26.11) * mm});
            skLineSegment(sketch, "E34.90.1", {"start": v(-0.5, 26.54) * mm, "end": v(-0.9, 26.53) * mm});
            skLineSegment(sketch, "E34.90.2", {"start": v(-0.02, 26.15) * mm, "end": v(-0.5, 26.54) * mm});
            skLineSegment(sketch, "E34.91.0", {"start": v(0.5, 26.54) * mm, "end": v(-0.03, 26.15) * mm});
            skLineSegment(sketch, "E34.91.1", {"start": v(0.9, 26.53) * mm, "end": v(0.5, 26.54) * mm});
            skLineSegment(sketch, "E34.91.2", {"start": v(1.35, 26.11) * mm, "end": v(0.9, 26.53) * mm});
            skLineSegment(sketch, "E34.92.0", {"start": v(1.88, 26.48) * mm, "end": v(1.34, 26.11) * mm});
            skLineSegment(sketch, "E34.92.1", {"start": v(2.28, 26.45) * mm, "end": v(1.88, 26.48) * mm});
            skLineSegment(sketch, "E34.92.2", {"start": v(2.7, 26) * mm, "end": v(2.28, 26.45) * mm});
            skLineSegment(sketch, "E34.93.0", {"start": v(3.27, 26.34) * mm, "end": v(2.7, 26) * mm});
            skLineSegment(sketch, "E34.93.1", {"start": v(3.66, 26.29) * mm, "end": v(3.27, 26.34) * mm});
            skLineSegment(sketch, "E34.93.2", {"start": v(4.07, 25.82) * mm, "end": v(3.66, 26.29) * mm});
            skLineSegment(sketch, "E34.94.0", {"start": v(4.64, 26.13) * mm, "end": v(4.06, 25.82) * mm});
            skLineSegment(sketch, "E34.94.1", {"start": v(5.03, 26.06) * mm, "end": v(4.64, 26.13) * mm});
            skLineSegment(sketch, "E34.94.2", {"start": v(5.41, 25.57) * mm, "end": v(5.03, 26.06) * mm});
            skLineSegment(sketch, "E34.95.0", {"start": v(6, 25.85) * mm, "end": v(5.4, 25.57) * mm});
            skLineSegment(sketch, "E34.95.1", {"start": v(6.39, 25.76) * mm, "end": v(6, 25.85) * mm});
            skLineSegment(sketch, "E34.95.2", {"start": v(6.74, 25.25) * mm, "end": v(6.39, 25.76) * mm});
            skLineSegment(sketch, "E34.96.0", {"start": v(7.34, 25.5) * mm, "end": v(6.73, 25.26) * mm});
            skLineSegment(sketch, "E34.96.1", {"start": v(7.73, 25.39) * mm, "end": v(7.34, 25.5) * mm});
            skLineSegment(sketch, "E34.96.2", {"start": v(8.05, 24.86) * mm, "end": v(7.73, 25.39) * mm});
            skLineSegment(sketch, "E34.97.0", {"start": v(8.67, 25.08) * mm, "end": v(8.05, 24.87) * mm});
            skLineSegment(sketch, "E34.97.1", {"start": v(9.04, 24.95) * mm, "end": v(8.67, 25.08) * mm});
            skLineSegment(sketch, "E34.97.2", {"start": v(9.34, 24.4) * mm, "end": v(9.04, 24.95) * mm});
            skLineSegment(sketch, "E34.98.0", {"start": v(9.97, 24.6) * mm, "end": v(9.34, 24.4) * mm});
            skLineSegment(sketch, "E34.98.1", {"start": v(10.34, 24.44) * mm, "end": v(9.97, 24.6) * mm});
            skLineSegment(sketch, "E34.98.2", {"start": v(10.6, 23.88) * mm, "end": v(10.34, 24.44) * mm});
            skLineSegment(sketch, "E34.99.0", {"start": v(11.24, 24.03) * mm, "end": v(10.6, 23.89) * mm});
            skLineSegment(sketch, "E34.99.1", {"start": v(11.6, 23.86) * mm, "end": v(11.24, 24.03) * mm});
            skLineSegment(sketch, "E34.99.2", {"start": v(11.84, 23.3) * mm, "end": v(11.6, 23.86) * mm});
            skLineSegment(sketch, "E34.100.0", {"start": v(12.48, 23.4) * mm, "end": v(11.83, 23.3) * mm});
            skLineSegment(sketch, "E34.100.1", {"start": v(12.83, 23.22) * mm, "end": v(12.48, 23.4) * mm});
            skLineSegment(sketch, "E34.100.2", {"start": v(13.04, 22.64) * mm, "end": v(12.83, 23.22) * mm});
            skLineSegment(sketch, "E34.101.0", {"start": v(13.69, 22.72) * mm, "end": v(13.04, 22.64) * mm});
            skLineSegment(sketch, "E34.101.1", {"start": v(14.03, 22.51) * mm, "end": v(13.69, 22.72) * mm});
            skLineSegment(sketch, "E34.101.2", {"start": v(14.2, 21.92) * mm, "end": v(14.03, 22.51) * mm});
            skLineSegment(sketch, "E34.102.0", {"start": v(14.86, 21.97) * mm, "end": v(14.2, 21.93) * mm});
            skLineSegment(sketch, "E34.102.1", {"start": v(15.19, 21.75) * mm, "end": v(14.86, 21.97) * mm});
            skLineSegment(sketch, "E34.102.2", {"start": v(15.34, 21.15) * mm, "end": v(15.19, 21.75) * mm});
            skLineSegment(sketch, "E34.103.0", {"start": v(15.99, 21.16) * mm, "end": v(15.33, 21.15) * mm});
            skLineSegment(sketch, "E34.103.1", {"start": v(16.3, 20.92) * mm, "end": v(15.99, 21.16) * mm});
            skLineSegment(sketch, "E34.103.2", {"start": v(16.42, 20.32) * mm, "end": v(16.3, 20.92) * mm});
            skLineSegment(sketch, "E34.104.0", {"start": v(17.07, 20.3) * mm, "end": v(16.42, 20.32) * mm});
            skLineSegment(sketch, "E34.104.1", {"start": v(17.38, 20.04) * mm, "end": v(17.07, 20.3) * mm});
            skLineSegment(sketch, "E34.104.2", {"start": v(17.46, 19.43) * mm, "end": v(17.38, 20.04) * mm});
            skLineSegment(sketch, "E34.105.0", {"start": v(18.11, 19.37) * mm, "end": v(17.46, 19.43) * mm});
            skLineSegment(sketch, "E34.105.1", {"start": v(18.4, 19.1) * mm, "end": v(18.11, 19.37) * mm});
            skLineSegment(sketch, "E34.105.2", {"start": v(18.45, 18.48) * mm, "end": v(18.4, 19.1) * mm});
            skLineSegment(sketch, "E34.106.0", {"start": v(19.1, 18.4) * mm, "end": v(18.45, 18.49) * mm});
            skLineSegment(sketch, "E34.106.1", {"start": v(19.37, 18.1) * mm, "end": v(19.1, 18.4) * mm});
            skLineSegment(sketch, "E34.106.2", {"start": v(19.4, 17.5) * mm, "end": v(19.37, 18.1) * mm});
            skLineSegment(sketch, "E34.107.0", {"start": v(20.03, 17.37) * mm, "end": v(19.4, 17.5) * mm});
            skLineSegment(sketch, "E34.107.1", {"start": v(20.3, 17.07) * mm, "end": v(20.03, 17.37) * mm});
            skLineSegment(sketch, "E34.107.2", {"start": v(20.28, 16.45) * mm, "end": v(20.3, 17.07) * mm});
            skLineSegment(sketch, "E34.108.0", {"start": v(20.92, 16.3) * mm, "end": v(20.28, 16.45) * mm});
            skLineSegment(sketch, "E34.108.1", {"start": v(21.16, 15.98) * mm, "end": v(20.92, 16.3) * mm});
            skLineSegment(sketch, "E34.108.2", {"start": v(21.12, 15.36) * mm, "end": v(21.16, 15.98) * mm});
            skLineSegment(sketch, "E34.109.0", {"start": v(21.74, 15.18) * mm, "end": v(21.11, 15.37) * mm});
            skLineSegment(sketch, "E34.109.1", {"start": v(21.97, 14.85) * mm, "end": v(21.74, 15.18) * mm});
            skLineSegment(sketch, "E34.109.2", {"start": v(21.9, 14.24) * mm, "end": v(21.97, 14.85) * mm});
            skLineSegment(sketch, "E34.110.0", {"start": v(22.5, 14.02) * mm, "end": v(21.89, 14.24) * mm});
            skLineSegment(sketch, "E34.110.1", {"start": v(22.71, 13.68) * mm, "end": v(22.5, 14.02) * mm});
            skLineSegment(sketch, "E34.110.2", {"start": v(22.6, 13.07) * mm, "end": v(22.71, 13.68) * mm});
            skLineSegment(sketch, "E34.111.0", {"start": v(23.2, 12.82) * mm, "end": v(22.6, 13.07) * mm});
            skLineSegment(sketch, "E34.111.1", {"start": v(23.4, 12.47) * mm, "end": v(23.2, 12.82) * mm});
            skLineSegment(sketch, "E34.111.2", {"start": v(23.26, 11.87) * mm, "end": v(23.4, 12.47) * mm});
            skLineSegment(sketch, "E34.112.0", {"start": v(23.84, 11.58) * mm, "end": v(23.25, 11.87) * mm});
            skLineSegment(sketch, "E34.112.1", {"start": v(24.02, 11.22) * mm, "end": v(23.84, 11.58) * mm});
            skLineSegment(sketch, "E34.112.2", {"start": v(23.85, 10.63) * mm, "end": v(24.02, 11.22) * mm});
            skLineSegment(sketch, "E34.113.0", {"start": v(24.42, 10.32) * mm, "end": v(23.84, 10.64) * mm});
            skLineSegment(sketch, "E34.113.1", {"start": v(24.57, 9.95) * mm, "end": v(24.42, 10.32) * mm});
            skLineSegment(sketch, "E34.113.2", {"start": v(24.37, 9.37) * mm, "end": v(24.57, 9.95) * mm});
            skLineSegment(sketch, "E34.114.0", {"start": v(24.92, 9.03) * mm, "end": v(24.37, 9.37) * mm});
            skLineSegment(sketch, "E34.114.1", {"start": v(25.06, 8.65) * mm, "end": v(24.92, 9.03) * mm});
            skLineSegment(sketch, "E34.114.2", {"start": v(24.82, 8.08) * mm, "end": v(25.06, 8.65) * mm});
            skLineSegment(sketch, "E34.115.0", {"start": v(25.36, 7.7) * mm, "end": v(24.82, 8.08) * mm});
            skLineSegment(sketch, "E34.115.1", {"start": v(25.47, 7.32) * mm, "end": v(25.36, 7.7) * mm});
            skLineSegment(sketch, "E34.115.2", {"start": v(25.21, 6.76) * mm, "end": v(25.47, 7.32) * mm});
            skLineSegment(sketch, "E34.116.0", {"start": v(25.73, 6.37) * mm, "end": v(25.21, 6.77) * mm});
            skLineSegment(sketch, "E34.116.1", {"start": v(25.82, 5.98) * mm, "end": v(25.73, 6.37) * mm});
            skLineSegment(sketch, "E34.116.2", {"start": v(25.53, 5.43) * mm, "end": v(25.82, 5.98) * mm});
            skLineSegment(sketch, "E34.117.0", {"start": v(26.02, 5) * mm, "end": v(25.53, 5.44) * mm});
            skLineSegment(sketch, "E34.117.1", {"start": v(26.1, 4.62) * mm, "end": v(26.02, 5) * mm});
            skLineSegment(sketch, "E34.117.2", {"start": v(25.78, 4.09) * mm, "end": v(26.1, 4.62) * mm});
            skLineSegment(sketch, "E34.118.0", {"start": v(26.25, 3.64) * mm, "end": v(25.78, 4.1) * mm});
            skLineSegment(sketch, "E34.118.1", {"start": v(26.3, 3.24) * mm, "end": v(26.25, 3.64) * mm});
            skLineSegment(sketch, "E34.118.2", {"start": v(25.96, 2.73) * mm, "end": v(26.3, 3.24) * mm});
            skLineSegment(sketch, "E34.119.0", {"start": v(26.4, 2.26) * mm, "end": v(25.96, 2.74) * mm});
            skLineSegment(sketch, "E34.119.1", {"start": v(26.44, 1.86) * mm, "end": v(26.4, 2.26) * mm});
            skLineSegment(sketch, "E34.119.2", {"start": v(26.06, 1.37) * mm, "end": v(26.44, 1.86) * mm});
            skPoint(sketch, "E34.center", {"position": v(-0.04, 0.01) * mm});
            skLineSegment(sketch, "E34.anchor1", {"start": v(-0.04, 0.01) * mm, "end": v(26.49, 0.87) * mm, "construction": true});
            skLineSegment(sketch, "E34.anchor2", {"start": v(-0.04, 0.01) * mm, "end": v(26.4, 2.26) * mm, "construction": true});
            skSolve(sketch);
        }
        {
            var Q0;
            {var subQ37=sQuery(id+"F4.wireOp",EDGE,"E34.1.1");Q0=makeQuery(id+"F4.imprint","IMPRINT",FACE,{"disambiguationData":[TD([[makeQuery(id+"F4.imprint","IMPRINT",EDGE,{"derivedFrom":subQ37}),-1.0]])]});}
            var Q1;
            {var subQ0=sQuery(id+"F4.wireOp",EDGE,"E34.15.0");var subQ3=sQuery(id+"F4.wireOp",EDGE,"E29");var subQ4=makeQuery(id+"F4.imprint","INTERSECT",VERTEX,{"derivedFrom":[subQ3,subQ0]});Q1=makeQuery(id+"F4.imprint","IMPRINT",FACE,{"disambiguationData":[TD([[makeQuery(id+"F4.imprint","IMPRINT",EDGE,{"disambiguationData":[TD([[subQ4,-1.0]])],"derivedFrom":subQ3}),1.0]])]});}
            var Q2;
            {var subQ0=sQuery(id+"F4.wireOp",EDGE,"E34.16.0");var subQ1=sQuery(id+"F4.wireOp",EDGE,"E29");var subQ2=makeQuery(id+"F4.imprint","INTERSECT",VERTEX,{"derivedFrom":[subQ1,subQ0]});Q2=makeQuery(id+"F4.imprint","IMPRINT",FACE,{"disambiguationData":[TD([[makeQuery(id+"F4.imprint","IMPRINT",EDGE,{"disambiguationData":[TD([[subQ2,-1.0]])],"derivedFrom":subQ1}),1.0]])]});}
            var Q3;
            {var subQ0=sQuery(id+"F4.wireOp",EDGE,"E34.17.0");var subQ1=sQuery(id+"F4.wireOp",EDGE,"E29");var subQ2=makeQuery(id+"F4.imprint","INTERSECT",VERTEX,{"derivedFrom":[subQ1,subQ0]});Q3=makeQuery(id+"F4.imprint","IMPRINT",FACE,{"disambiguationData":[TD([[makeQuery(id+"F4.imprint","IMPRINT",EDGE,{"disambiguationData":[TD([[subQ2,-1.0]])],"derivedFrom":subQ1}),1.0]])]});}
            var Q4;
            {var subQ0=sQuery(id+"F4.wireOp",EDGE,"E34.18.0");var subQ1=sQuery(id+"F4.wireOp",EDGE,"E29");var subQ2=makeQuery(id+"F4.imprint","INTERSECT",VERTEX,{"derivedFrom":[subQ1,subQ0]});Q4=makeQuery(id+"F4.imprint","IMPRINT",FACE,{"disambiguationData":[TD([[makeQuery(id+"F4.imprint","IMPRINT",EDGE,{"disambiguationData":[TD([[subQ2,-1.0]])],"derivedFrom":subQ1}),1.0]])]});}
            var Q5;
            {var subQ0=sQuery(id+"F4.wireOp",EDGE,"E34.19.0");var subQ1=sQuery(id+"F4.wireOp",EDGE,"E29");var subQ2=makeQuery(id+"F4.imprint","INTERSECT",VERTEX,{"derivedFrom":[subQ1,subQ0]});Q5=makeQuery(id+"F4.imprint","IMPRINT",FACE,{"disambiguationData":[TD([[makeQuery(id+"F4.imprint","IMPRINT",EDGE,{"disambiguationData":[TD([[subQ2,-1.0]])],"derivedFrom":subQ1}),1.0]])]});}
            var Q6;
            {var subQ0=sQuery(id+"F4.wireOp",EDGE,"E34.20.0");var subQ1=sQuery(id+"F4.wireOp",EDGE,"E29");var subQ2=makeQuery(id+"F4.imprint","INTERSECT",VERTEX,{"derivedFrom":[subQ1,subQ0]});Q6=makeQuery(id+"F4.imprint","IMPRINT",FACE,{"disambiguationData":[TD([[makeQuery(id+"F4.imprint","IMPRINT",EDGE,{"disambiguationData":[TD([[subQ2,-1.0]])],"derivedFrom":subQ1}),1.0]])]});}
            var Q7;
            {var subQ0=sQuery(id+"F4.wireOp",EDGE,"E34.21.0");var subQ1=sQuery(id+"F4.wireOp",EDGE,"E29");var subQ2=makeQuery(id+"F4.imprint","INTERSECT",VERTEX,{"derivedFrom":[subQ1,subQ0]});Q7=makeQuery(id+"F4.imprint","IMPRINT",FACE,{"disambiguationData":[TD([[makeQuery(id+"F4.imprint","IMPRINT",EDGE,{"disambiguationData":[TD([[subQ2,-1.0]])],"derivedFrom":subQ1}),1.0]])]});}
            var Q8;
            {var subQ0=sQuery(id+"F4.wireOp",EDGE,"E34.22.0");var subQ1=sQuery(id+"F4.wireOp",EDGE,"E29");var subQ2=makeQuery(id+"F4.imprint","INTERSECT",VERTEX,{"derivedFrom":[subQ1,subQ0]});Q8=makeQuery(id+"F4.imprint","IMPRINT",FACE,{"disambiguationData":[TD([[makeQuery(id+"F4.imprint","IMPRINT",EDGE,{"disambiguationData":[TD([[subQ2,-1.0]])],"derivedFrom":subQ1}),1.0]])]});}
            var Q9;
            {var subQ0=sQuery(id+"F4.wireOp",EDGE,"E34.23.0");var subQ1=sQuery(id+"F4.wireOp",EDGE,"E29");var subQ2=makeQuery(id+"F4.imprint","INTERSECT",VERTEX,{"derivedFrom":[subQ1,subQ0]});Q9=makeQuery(id+"F4.imprint","IMPRINT",FACE,{"disambiguationData":[TD([[makeQuery(id+"F4.imprint","IMPRINT",EDGE,{"disambiguationData":[TD([[subQ2,-1.0]])],"derivedFrom":subQ1}),1.0]])]});}
            var Q10;
            {var subQ0=sQuery(id+"F4.wireOp",EDGE,"E34.24.0");var subQ1=sQuery(id+"F4.wireOp",EDGE,"E29");var subQ2=makeQuery(id+"F4.imprint","INTERSECT",VERTEX,{"derivedFrom":[subQ1,subQ0]});Q10=makeQuery(id+"F4.imprint","IMPRINT",FACE,{"disambiguationData":[TD([[makeQuery(id+"F4.imprint","IMPRINT",EDGE,{"disambiguationData":[TD([[subQ2,-1.0]])],"derivedFrom":subQ1}),1.0]])]});}
            var Q11;
            {var subQ0=sQuery(id+"F4.wireOp",EDGE,"E34.25.0");var subQ1=sQuery(id+"F4.wireOp",EDGE,"E29");var subQ2=makeQuery(id+"F4.imprint","INTERSECT",VERTEX,{"derivedFrom":[subQ1,subQ0]});Q11=makeQuery(id+"F4.imprint","IMPRINT",FACE,{"disambiguationData":[TD([[makeQuery(id+"F4.imprint","IMPRINT",EDGE,{"disambiguationData":[TD([[subQ2,-1.0]])],"derivedFrom":subQ1}),1.0]])]});}
            var Q12;
            {var subQ0=sQuery(id+"F4.wireOp",EDGE,"E34.26.0");var subQ1=sQuery(id+"F4.wireOp",EDGE,"E29");var subQ2=makeQuery(id+"F4.imprint","INTERSECT",VERTEX,{"derivedFrom":[subQ1,subQ0]});Q12=makeQuery(id+"F4.imprint","IMPRINT",FACE,{"disambiguationData":[TD([[makeQuery(id+"F4.imprint","IMPRINT",EDGE,{"disambiguationData":[TD([[subQ2,-1.0]])],"derivedFrom":subQ1}),1.0]])]});}
            var Q13;
            {var subQ1=sQuery(id+"F4.wireOp",EDGE,"E29");var subQ3=sQuery(id+"F4.wireOp",EDGE,"E34.27.0");var subQ5=makeQuery(id+"F4.imprint","INTERSECT",VERTEX,{"derivedFrom":[subQ1,subQ3]});Q13=makeQuery(id+"F4.imprint","IMPRINT",FACE,{"disambiguationData":[TD([[makeQuery(id+"F4.imprint","IMPRINT",EDGE,{"disambiguationData":[TD([[subQ5,-1.0]])],"derivedFrom":subQ1}),1.0]])]});}
            var Q14;
            {var subQ1=sQuery(id+"F4.wireOp",EDGE,"E29");var subQ3=sQuery(id+"F4.wireOp",EDGE,"E34.28.0");var subQ5=makeQuery(id+"F4.imprint","INTERSECT",VERTEX,{"derivedFrom":[subQ1,subQ3]});Q14=makeQuery(id+"F4.imprint","IMPRINT",FACE,{"disambiguationData":[TD([[makeQuery(id+"F4.imprint","IMPRINT",EDGE,{"disambiguationData":[TD([[subQ5,-1.0]])],"derivedFrom":subQ1}),1.0]])]});}
            var Q15;
            {var subQ0=sQuery(id+"F4.wireOp",EDGE,"E34.29.0");var subQ1=sQuery(id+"F4.wireOp",EDGE,"E29");var subQ2=makeQuery(id+"F4.imprint","INTERSECT",VERTEX,{"derivedFrom":[subQ1,subQ0]});Q15=makeQuery(id+"F4.imprint","IMPRINT",FACE,{"disambiguationData":[TD([[makeQuery(id+"F4.imprint","IMPRINT",EDGE,{"disambiguationData":[TD([[subQ2,-1.0]])],"derivedFrom":subQ1}),1.0]])]});}
            var Q16;
            {var subQ0=sQuery(id+"F4.wireOp",EDGE,"E34.30.0");var subQ1=sQuery(id+"F4.wireOp",EDGE,"E29");var subQ2=makeQuery(id+"F4.imprint","INTERSECT",VERTEX,{"derivedFrom":[subQ1,subQ0]});Q16=makeQuery(id+"F4.imprint","IMPRINT",FACE,{"disambiguationData":[TD([[makeQuery(id+"F4.imprint","IMPRINT",EDGE,{"disambiguationData":[TD([[subQ2,-1.0]])],"derivedFrom":subQ1}),1.0]])]});}
            var Q17;
            {var subQ1=sQuery(id+"F4.wireOp",EDGE,"E29");var subQ3=sQuery(id+"F4.wireOp",EDGE,"E34.31.0");var subQ5=makeQuery(id+"F4.imprint","INTERSECT",VERTEX,{"derivedFrom":[subQ1,subQ3]});Q17=makeQuery(id+"F4.imprint","IMPRINT",FACE,{"disambiguationData":[TD([[makeQuery(id+"F4.imprint","IMPRINT",EDGE,{"disambiguationData":[TD([[subQ5,-1.0]])],"derivedFrom":subQ1}),1.0]])]});}
            var Q18;
            {var subQ1=sQuery(id+"F4.wireOp",EDGE,"E29");var subQ3=sQuery(id+"F4.wireOp",EDGE,"E34.32.0");var subQ5=makeQuery(id+"F4.imprint","INTERSECT",VERTEX,{"derivedFrom":[subQ1,subQ3]});Q18=makeQuery(id+"F4.imprint","IMPRINT",FACE,{"disambiguationData":[TD([[makeQuery(id+"F4.imprint","IMPRINT",EDGE,{"disambiguationData":[TD([[subQ5,-1.0]])],"derivedFrom":subQ1}),1.0]])]});}
            var Q19;
            {var subQ0=sQuery(id+"F4.wireOp",EDGE,"E34.33.0");var subQ1=sQuery(id+"F4.wireOp",EDGE,"E29");var subQ2=makeQuery(id+"F4.imprint","INTERSECT",VERTEX,{"derivedFrom":[subQ1,subQ0]});Q19=makeQuery(id+"F4.imprint","IMPRINT",FACE,{"disambiguationData":[TD([[makeQuery(id+"F4.imprint","IMPRINT",EDGE,{"disambiguationData":[TD([[subQ2,-1.0]])],"derivedFrom":subQ1}),1.0]])]});}
            var Q20;
            {var subQ0=sQuery(id+"F4.wireOp",EDGE,"E34.34.0");var subQ1=sQuery(id+"F4.wireOp",EDGE,"E29");var subQ2=makeQuery(id+"F4.imprint","INTERSECT",VERTEX,{"derivedFrom":[subQ1,subQ0]});Q20=makeQuery(id+"F4.imprint","IMPRINT",FACE,{"disambiguationData":[TD([[makeQuery(id+"F4.imprint","IMPRINT",EDGE,{"disambiguationData":[TD([[subQ2,-1.0]])],"derivedFrom":subQ1}),1.0]])]});}
            var Q21;
            {var subQ0=sQuery(id+"F4.wireOp",EDGE,"E34.35.0");var subQ1=sQuery(id+"F4.wireOp",EDGE,"E29");var subQ2=makeQuery(id+"F4.imprint","INTERSECT",VERTEX,{"derivedFrom":[subQ1,subQ0]});Q21=makeQuery(id+"F4.imprint","IMPRINT",FACE,{"disambiguationData":[TD([[makeQuery(id+"F4.imprint","IMPRINT",EDGE,{"disambiguationData":[TD([[subQ2,-1.0]])],"derivedFrom":subQ1}),1.0]])]});}
            var Q22;
            {var subQ0=sQuery(id+"F4.wireOp",EDGE,"E34.36.0");var subQ1=sQuery(id+"F4.wireOp",EDGE,"E29");var subQ2=makeQuery(id+"F4.imprint","INTERSECT",VERTEX,{"derivedFrom":[subQ1,subQ0]});Q22=makeQuery(id+"F4.imprint","IMPRINT",FACE,{"disambiguationData":[TD([[makeQuery(id+"F4.imprint","IMPRINT",EDGE,{"disambiguationData":[TD([[subQ2,-1.0]])],"derivedFrom":subQ1}),1.0]])]});}
            var Q23;
            {var subQ0=sQuery(id+"F4.wireOp",EDGE,"E34.37.0");var subQ1=sQuery(id+"F4.wireOp",EDGE,"E29");var subQ2=makeQuery(id+"F4.imprint","INTERSECT",VERTEX,{"derivedFrom":[subQ1,subQ0]});Q23=makeQuery(id+"F4.imprint","IMPRINT",FACE,{"disambiguationData":[TD([[makeQuery(id+"F4.imprint","IMPRINT",EDGE,{"disambiguationData":[TD([[subQ2,-1.0]])],"derivedFrom":subQ1}),1.0]])]});}
            var Q24;
            {var subQ0=sQuery(id+"F4.wireOp",EDGE,"E34.38.0");var subQ1=sQuery(id+"F4.wireOp",EDGE,"E29");var subQ2=makeQuery(id+"F4.imprint","INTERSECT",VERTEX,{"derivedFrom":[subQ1,subQ0]});Q24=makeQuery(id+"F4.imprint","IMPRINT",FACE,{"disambiguationData":[TD([[makeQuery(id+"F4.imprint","IMPRINT",EDGE,{"disambiguationData":[TD([[subQ2,-1.0]])],"derivedFrom":subQ1}),1.0]])]});}
            var Q25;
            {var subQ0=sQuery(id+"F4.wireOp",EDGE,"E34.39.0");var subQ1=sQuery(id+"F4.wireOp",EDGE,"E29");var subQ2=makeQuery(id+"F4.imprint","INTERSECT",VERTEX,{"derivedFrom":[subQ1,subQ0]});Q25=makeQuery(id+"F4.imprint","IMPRINT",FACE,{"disambiguationData":[TD([[makeQuery(id+"F4.imprint","IMPRINT",EDGE,{"disambiguationData":[TD([[subQ2,-1.0]])],"derivedFrom":subQ1}),1.0]])]});}
            var Q26;
            {var subQ0=sQuery(id+"F4.wireOp",EDGE,"E34.40.0");var subQ1=sQuery(id+"F4.wireOp",EDGE,"E29");var subQ2=makeQuery(id+"F4.imprint","INTERSECT",VERTEX,{"derivedFrom":[subQ1,subQ0]});Q26=makeQuery(id+"F4.imprint","IMPRINT",FACE,{"disambiguationData":[TD([[makeQuery(id+"F4.imprint","IMPRINT",EDGE,{"disambiguationData":[TD([[subQ2,-1.0]])],"derivedFrom":subQ1}),1.0]])]});}
            var Q27;
            {var subQ0=sQuery(id+"F4.wireOp",EDGE,"E34.41.0");var subQ1=sQuery(id+"F4.wireOp",EDGE,"E29");var subQ2=makeQuery(id+"F4.imprint","INTERSECT",VERTEX,{"derivedFrom":[subQ1,subQ0]});Q27=makeQuery(id+"F4.imprint","IMPRINT",FACE,{"disambiguationData":[TD([[makeQuery(id+"F4.imprint","IMPRINT",EDGE,{"disambiguationData":[TD([[subQ2,-1.0]])],"derivedFrom":subQ1}),1.0]])]});}
            var Q28;
            {var subQ0=sQuery(id+"F4.wireOp",EDGE,"E34.42.0");var subQ1=sQuery(id+"F4.wireOp",EDGE,"E29");var subQ2=makeQuery(id+"F4.imprint","INTERSECT",VERTEX,{"derivedFrom":[subQ1,subQ0]});Q28=makeQuery(id+"F4.imprint","IMPRINT",FACE,{"disambiguationData":[TD([[makeQuery(id+"F4.imprint","IMPRINT",EDGE,{"disambiguationData":[TD([[subQ2,-1.0]])],"derivedFrom":subQ1}),1.0]])]});}
            var Q29;
            {var subQ0=sQuery(id+"F4.wireOp",EDGE,"E34.43.0");var subQ1=sQuery(id+"F4.wireOp",EDGE,"E29");var subQ2=makeQuery(id+"F4.imprint","INTERSECT",VERTEX,{"derivedFrom":[subQ1,subQ0]});Q29=makeQuery(id+"F4.imprint","IMPRINT",FACE,{"disambiguationData":[TD([[makeQuery(id+"F4.imprint","IMPRINT",EDGE,{"disambiguationData":[TD([[subQ2,-1.0]])],"derivedFrom":subQ1}),1.0]])]});}
            var Q30;
            {var subQ0=sQuery(id+"F4.wireOp",EDGE,"E34.44.0");var subQ1=sQuery(id+"F4.wireOp",EDGE,"E29");var subQ2=makeQuery(id+"F4.imprint","INTERSECT",VERTEX,{"derivedFrom":[subQ1,subQ0]});Q30=makeQuery(id+"F4.imprint","IMPRINT",FACE,{"disambiguationData":[TD([[makeQuery(id+"F4.imprint","IMPRINT",EDGE,{"disambiguationData":[TD([[subQ2,-1.0]])],"derivedFrom":subQ1}),1.0]])]});}
            var Q31;
            {var subQ0=sQuery(id+"F4.wireOp",EDGE,"E34.45.0");var subQ1=sQuery(id+"F4.wireOp",EDGE,"E29");var subQ2=makeQuery(id+"F4.imprint","INTERSECT",VERTEX,{"derivedFrom":[subQ1,subQ0]});Q31=makeQuery(id+"F4.imprint","IMPRINT",FACE,{"disambiguationData":[TD([[makeQuery(id+"F4.imprint","IMPRINT",EDGE,{"disambiguationData":[TD([[subQ2,-1.0]])],"derivedFrom":subQ1}),1.0]])]});}
            var Q32;
            {var subQ0=sQuery(id+"F4.wireOp",EDGE,"E34.46.0");var subQ1=sQuery(id+"F4.wireOp",EDGE,"E29");var subQ2=makeQuery(id+"F4.imprint","INTERSECT",VERTEX,{"derivedFrom":[subQ1,subQ0]});Q32=makeQuery(id+"F4.imprint","IMPRINT",FACE,{"disambiguationData":[TD([[makeQuery(id+"F4.imprint","IMPRINT",EDGE,{"disambiguationData":[TD([[subQ2,-1.0]])],"derivedFrom":subQ1}),1.0]])]});}
            var Q33;
            {var subQ0=sQuery(id+"F4.wireOp",EDGE,"E34.47.0");var subQ1=sQuery(id+"F4.wireOp",EDGE,"E29");var subQ2=makeQuery(id+"F4.imprint","INTERSECT",VERTEX,{"derivedFrom":[subQ1,subQ0]});Q33=makeQuery(id+"F4.imprint","IMPRINT",FACE,{"disambiguationData":[TD([[makeQuery(id+"F4.imprint","IMPRINT",EDGE,{"disambiguationData":[TD([[subQ2,-1.0]])],"derivedFrom":subQ1}),1.0]])]});}
            var Q34;
            {var subQ0=sQuery(id+"F4.wireOp",EDGE,"E34.48.0");var subQ1=sQuery(id+"F4.wireOp",EDGE,"E29");var subQ2=makeQuery(id+"F4.imprint","INTERSECT",VERTEX,{"derivedFrom":[subQ1,subQ0]});Q34=makeQuery(id+"F4.imprint","IMPRINT",FACE,{"disambiguationData":[TD([[makeQuery(id+"F4.imprint","IMPRINT",EDGE,{"disambiguationData":[TD([[subQ2,-1.0]])],"derivedFrom":subQ1}),1.0]])]});}
            var Q35;
            {var subQ0=sQuery(id+"F4.wireOp",EDGE,"E34.49.0");var subQ1=sQuery(id+"F4.wireOp",EDGE,"E29");var subQ2=makeQuery(id+"F4.imprint","INTERSECT",VERTEX,{"derivedFrom":[subQ1,subQ0]});Q35=makeQuery(id+"F4.imprint","IMPRINT",FACE,{"disambiguationData":[TD([[makeQuery(id+"F4.imprint","IMPRINT",EDGE,{"disambiguationData":[TD([[subQ2,-1.0]])],"derivedFrom":subQ1}),1.0]])]});}
            var Q36;
            {var subQ0=sQuery(id+"F4.wireOp",EDGE,"E34.50.0");var subQ1=sQuery(id+"F4.wireOp",EDGE,"E29");var subQ2=makeQuery(id+"F4.imprint","INTERSECT",VERTEX,{"derivedFrom":[subQ1,subQ0]});Q36=makeQuery(id+"F4.imprint","IMPRINT",FACE,{"disambiguationData":[TD([[makeQuery(id+"F4.imprint","IMPRINT",EDGE,{"disambiguationData":[TD([[subQ2,-1.0]])],"derivedFrom":subQ1}),1.0]])]});}
            var Q37;
            {var subQ0=sQuery(id+"F4.wireOp",EDGE,"E34.51.0");var subQ1=sQuery(id+"F4.wireOp",EDGE,"E29");var subQ2=makeQuery(id+"F4.imprint","INTERSECT",VERTEX,{"derivedFrom":[subQ1,subQ0]});Q37=makeQuery(id+"F4.imprint","IMPRINT",FACE,{"disambiguationData":[TD([[makeQuery(id+"F4.imprint","IMPRINT",EDGE,{"disambiguationData":[TD([[subQ2,-1.0]])],"derivedFrom":subQ1}),1.0]])]});}
            var Q38;
            {var subQ0=sQuery(id+"F4.wireOp",EDGE,"E34.52.0");var subQ1=sQuery(id+"F4.wireOp",EDGE,"E29");var subQ2=makeQuery(id+"F4.imprint","INTERSECT",VERTEX,{"derivedFrom":[subQ1,subQ0]});Q38=makeQuery(id+"F4.imprint","IMPRINT",FACE,{"disambiguationData":[TD([[makeQuery(id+"F4.imprint","IMPRINT",EDGE,{"disambiguationData":[TD([[subQ2,-1.0]])],"derivedFrom":subQ1}),1.0]])]});}
            var Q39;
            {var subQ0=sQuery(id+"F4.wireOp",EDGE,"E34.53.0");var subQ1=sQuery(id+"F4.wireOp",EDGE,"E29");var subQ2=makeQuery(id+"F4.imprint","INTERSECT",VERTEX,{"derivedFrom":[subQ1,subQ0]});Q39=makeQuery(id+"F4.imprint","IMPRINT",FACE,{"disambiguationData":[TD([[makeQuery(id+"F4.imprint","IMPRINT",EDGE,{"disambiguationData":[TD([[subQ2,-1.0]])],"derivedFrom":subQ1}),1.0]])]});}
            var Q40;
            {var subQ0=sQuery(id+"F4.wireOp",EDGE,"E34.54.0");var subQ1=sQuery(id+"F4.wireOp",EDGE,"E29");var subQ2=makeQuery(id+"F4.imprint","INTERSECT",VERTEX,{"derivedFrom":[subQ1,subQ0]});Q40=makeQuery(id+"F4.imprint","IMPRINT",FACE,{"disambiguationData":[TD([[makeQuery(id+"F4.imprint","IMPRINT",EDGE,{"disambiguationData":[TD([[subQ2,-1.0]])],"derivedFrom":subQ1}),1.0]])]});}
            var Q41;
            {var subQ0=sQuery(id+"F4.wireOp",EDGE,"E34.55.0");var subQ1=sQuery(id+"F4.wireOp",EDGE,"E29");var subQ2=makeQuery(id+"F4.imprint","INTERSECT",VERTEX,{"derivedFrom":[subQ1,subQ0]});Q41=makeQuery(id+"F4.imprint","IMPRINT",FACE,{"disambiguationData":[TD([[makeQuery(id+"F4.imprint","IMPRINT",EDGE,{"disambiguationData":[TD([[subQ2,-1.0]])],"derivedFrom":subQ1}),1.0]])]});}
            var Q42;
            {var subQ1=sQuery(id+"F4.wireOp",EDGE,"E29");var subQ3=sQuery(id+"F4.wireOp",EDGE,"E34.56.0");var subQ5=makeQuery(id+"F4.imprint","INTERSECT",VERTEX,{"derivedFrom":[subQ1,subQ3]});Q42=makeQuery(id+"F4.imprint","IMPRINT",FACE,{"disambiguationData":[TD([[makeQuery(id+"F4.imprint","IMPRINT",EDGE,{"disambiguationData":[TD([[subQ5,-1.0]])],"derivedFrom":subQ1}),1.0]])]});}
            var Q43;
            {var subQ0=sQuery(id+"F4.wireOp",EDGE,"E34.58.0");var subQ1=sQuery(id+"F4.wireOp",EDGE,"E29");var subQ2=makeQuery(id+"F4.imprint","INTERSECT",VERTEX,{"derivedFrom":[subQ1,subQ0]});Q43=makeQuery(id+"F4.imprint","IMPRINT",FACE,{"disambiguationData":[TD([[makeQuery(id+"F4.imprint","IMPRINT",EDGE,{"disambiguationData":[TD([[subQ2,-1.0]])],"derivedFrom":subQ1}),1.0]])]});}
            var Q44;
            {var subQ0=sQuery(id+"F4.wireOp",EDGE,"E34.59.0");var subQ1=sQuery(id+"F4.wireOp",EDGE,"E29");var subQ2=makeQuery(id+"F4.imprint","INTERSECT",VERTEX,{"derivedFrom":[subQ1,subQ0]});Q44=makeQuery(id+"F4.imprint","IMPRINT",FACE,{"disambiguationData":[TD([[makeQuery(id+"F4.imprint","IMPRINT",EDGE,{"disambiguationData":[TD([[subQ2,-1.0]])],"derivedFrom":subQ1}),1.0]])]});}
            var Q45;
            {var subQ0=sQuery(id+"F4.wireOp",EDGE,"E34.60.0");var subQ1=sQuery(id+"F4.wireOp",EDGE,"E29");var subQ2=makeQuery(id+"F4.imprint","INTERSECT",VERTEX,{"derivedFrom":[subQ1,subQ0]});Q45=makeQuery(id+"F4.imprint","IMPRINT",FACE,{"disambiguationData":[TD([[makeQuery(id+"F4.imprint","IMPRINT",EDGE,{"disambiguationData":[TD([[subQ2,-1.0]])],"derivedFrom":subQ1}),1.0]])]});}
            var Q46;
            {var subQ0=sQuery(id+"F4.wireOp",EDGE,"E34.61.0");var subQ1=sQuery(id+"F4.wireOp",EDGE,"E29");var subQ2=makeQuery(id+"F4.imprint","INTERSECT",VERTEX,{"derivedFrom":[subQ1,subQ0]});Q46=makeQuery(id+"F4.imprint","IMPRINT",FACE,{"disambiguationData":[TD([[makeQuery(id+"F4.imprint","IMPRINT",EDGE,{"disambiguationData":[TD([[subQ2,-1.0]])],"derivedFrom":subQ1}),1.0]])]});}
            var Q47;
            {var subQ0=sQuery(id+"F4.wireOp",EDGE,"E34.62.0");var subQ1=sQuery(id+"F4.wireOp",EDGE,"E29");var subQ2=makeQuery(id+"F4.imprint","INTERSECT",VERTEX,{"derivedFrom":[subQ1,subQ0]});Q47=makeQuery(id+"F4.imprint","IMPRINT",FACE,{"disambiguationData":[TD([[makeQuery(id+"F4.imprint","IMPRINT",EDGE,{"disambiguationData":[TD([[subQ2,-1.0]])],"derivedFrom":subQ1}),1.0]])]});}
            var Q48;
            {var subQ0=sQuery(id+"F4.wireOp",EDGE,"E34.63.0");var subQ1=sQuery(id+"F4.wireOp",EDGE,"E29");var subQ2=makeQuery(id+"F4.imprint","INTERSECT",VERTEX,{"derivedFrom":[subQ1,subQ0]});Q48=makeQuery(id+"F4.imprint","IMPRINT",FACE,{"disambiguationData":[TD([[makeQuery(id+"F4.imprint","IMPRINT",EDGE,{"disambiguationData":[TD([[subQ2,-1.0]])],"derivedFrom":subQ1}),1.0]])]});}
            var Q49;
            {var subQ0=sQuery(id+"F4.wireOp",EDGE,"E34.64.0");var subQ1=sQuery(id+"F4.wireOp",EDGE,"E29");var subQ2=makeQuery(id+"F4.imprint","INTERSECT",VERTEX,{"derivedFrom":[subQ1,subQ0]});Q49=makeQuery(id+"F4.imprint","IMPRINT",FACE,{"disambiguationData":[TD([[makeQuery(id+"F4.imprint","IMPRINT",EDGE,{"disambiguationData":[TD([[subQ2,-1.0]])],"derivedFrom":subQ1}),1.0]])]});}
            var Q50;
            {var subQ0=sQuery(id+"F4.wireOp",EDGE,"E34.57.0");var subQ1=sQuery(id+"F4.wireOp",EDGE,"E29");var subQ2=makeQuery(id+"F4.imprint","INTERSECT",VERTEX,{"derivedFrom":[subQ1,subQ0]});Q50=makeQuery(id+"F4.imprint","IMPRINT",FACE,{"disambiguationData":[TD([[makeQuery(id+"F4.imprint","IMPRINT",EDGE,{"disambiguationData":[TD([[subQ2,-1.0]])],"derivedFrom":subQ1}),1.0]])]});}
            var Q51;
            {var subQ0=sQuery(id+"F4.wireOp",EDGE,"E34.65.0");var subQ1=sQuery(id+"F4.wireOp",EDGE,"E29");var subQ2=makeQuery(id+"F4.imprint","INTERSECT",VERTEX,{"derivedFrom":[subQ1,subQ0]});Q51=makeQuery(id+"F4.imprint","IMPRINT",FACE,{"disambiguationData":[TD([[makeQuery(id+"F4.imprint","IMPRINT",EDGE,{"disambiguationData":[TD([[subQ2,-1.0]])],"derivedFrom":subQ1}),1.0]])]});}
            var Q52;
            {var subQ0=sQuery(id+"F4.wireOp",EDGE,"E34.66.0");var subQ1=sQuery(id+"F4.wireOp",EDGE,"E29");var subQ2=makeQuery(id+"F4.imprint","INTERSECT",VERTEX,{"derivedFrom":[subQ1,subQ0]});Q52=makeQuery(id+"F4.imprint","IMPRINT",FACE,{"disambiguationData":[TD([[makeQuery(id+"F4.imprint","IMPRINT",EDGE,{"disambiguationData":[TD([[subQ2,-1.0]])],"derivedFrom":subQ1}),1.0]])]});}
            var Q53;
            {var subQ0=sQuery(id+"F4.wireOp",EDGE,"E34.67.0");var subQ1=sQuery(id+"F4.wireOp",EDGE,"E29");var subQ2=makeQuery(id+"F4.imprint","INTERSECT",VERTEX,{"derivedFrom":[subQ1,subQ0]});Q53=makeQuery(id+"F4.imprint","IMPRINT",FACE,{"disambiguationData":[TD([[makeQuery(id+"F4.imprint","IMPRINT",EDGE,{"disambiguationData":[TD([[subQ2,-1.0]])],"derivedFrom":subQ1}),1.0]])]});}
            var Q54;
            {var subQ0=sQuery(id+"F4.wireOp",EDGE,"E34.68.0");var subQ1=sQuery(id+"F4.wireOp",EDGE,"E29");var subQ2=makeQuery(id+"F4.imprint","INTERSECT",VERTEX,{"derivedFrom":[subQ1,subQ0]});Q54=makeQuery(id+"F4.imprint","IMPRINT",FACE,{"disambiguationData":[TD([[makeQuery(id+"F4.imprint","IMPRINT",EDGE,{"disambiguationData":[TD([[subQ2,-1.0]])],"derivedFrom":subQ1}),1.0]])]});}
            var Q55;
            {var subQ0=sQuery(id+"F4.wireOp",EDGE,"E34.69.0");var subQ1=sQuery(id+"F4.wireOp",EDGE,"E29");var subQ2=makeQuery(id+"F4.imprint","INTERSECT",VERTEX,{"derivedFrom":[subQ1,subQ0]});Q55=makeQuery(id+"F4.imprint","IMPRINT",FACE,{"disambiguationData":[TD([[makeQuery(id+"F4.imprint","IMPRINT",EDGE,{"disambiguationData":[TD([[subQ2,-1.0]])],"derivedFrom":subQ1}),1.0]])]});}
            var Q56;
            {var subQ0=sQuery(id+"F4.wireOp",EDGE,"E34.70.0");var subQ1=sQuery(id+"F4.wireOp",EDGE,"E29");var subQ2=makeQuery(id+"F4.imprint","INTERSECT",VERTEX,{"derivedFrom":[subQ1,subQ0]});Q56=makeQuery(id+"F4.imprint","IMPRINT",FACE,{"disambiguationData":[TD([[makeQuery(id+"F4.imprint","IMPRINT",EDGE,{"disambiguationData":[TD([[subQ2,-1.0]])],"derivedFrom":subQ1}),1.0]])]});}
            var Q57;
            {var subQ0=sQuery(id+"F4.wireOp",EDGE,"E34.71.0");var subQ1=sQuery(id+"F4.wireOp",EDGE,"E29");var subQ2=makeQuery(id+"F4.imprint","INTERSECT",VERTEX,{"derivedFrom":[subQ1,subQ0]});Q57=makeQuery(id+"F4.imprint","IMPRINT",FACE,{"disambiguationData":[TD([[makeQuery(id+"F4.imprint","IMPRINT",EDGE,{"disambiguationData":[TD([[subQ2,-1.0]])],"derivedFrom":subQ1}),1.0]])]});}
            var Q58;
            {var subQ0=sQuery(id+"F4.wireOp",EDGE,"E34.72.0");var subQ1=sQuery(id+"F4.wireOp",EDGE,"E29");var subQ2=makeQuery(id+"F4.imprint","INTERSECT",VERTEX,{"derivedFrom":[subQ1,subQ0]});Q58=makeQuery(id+"F4.imprint","IMPRINT",FACE,{"disambiguationData":[TD([[makeQuery(id+"F4.imprint","IMPRINT",EDGE,{"disambiguationData":[TD([[subQ2,-1.0]])],"derivedFrom":subQ1}),1.0]])]});}
            var Q59;
            {var subQ0=sQuery(id+"F4.wireOp",EDGE,"E34.73.0");var subQ1=sQuery(id+"F4.wireOp",EDGE,"E29");var subQ2=makeQuery(id+"F4.imprint","INTERSECT",VERTEX,{"derivedFrom":[subQ1,subQ0]});Q59=makeQuery(id+"F4.imprint","IMPRINT",FACE,{"disambiguationData":[TD([[makeQuery(id+"F4.imprint","IMPRINT",EDGE,{"disambiguationData":[TD([[subQ2,-1.0]])],"derivedFrom":subQ1}),1.0]])]});}
            var Q60;
            {var subQ0=sQuery(id+"F4.wireOp",EDGE,"E34.74.0");var subQ1=sQuery(id+"F4.wireOp",EDGE,"E29");var subQ2=makeQuery(id+"F4.imprint","INTERSECT",VERTEX,{"derivedFrom":[subQ1,subQ0]});Q60=makeQuery(id+"F4.imprint","IMPRINT",FACE,{"disambiguationData":[TD([[makeQuery(id+"F4.imprint","IMPRINT",EDGE,{"disambiguationData":[TD([[subQ2,-1.0]])],"derivedFrom":subQ1}),1.0]])]});}
            var Q61;
            {var subQ0=sQuery(id+"F4.wireOp",EDGE,"E34.75.0");var subQ1=sQuery(id+"F4.wireOp",EDGE,"E29");var subQ2=makeQuery(id+"F4.imprint","INTERSECT",VERTEX,{"derivedFrom":[subQ1,subQ0]});Q61=makeQuery(id+"F4.imprint","IMPRINT",FACE,{"disambiguationData":[TD([[makeQuery(id+"F4.imprint","IMPRINT",EDGE,{"disambiguationData":[TD([[subQ2,-1.0]])],"derivedFrom":subQ1}),1.0]])]});}
            var Q62;
            {var subQ0=sQuery(id+"F4.wireOp",EDGE,"E34.76.0");var subQ1=sQuery(id+"F4.wireOp",EDGE,"E29");var subQ2=makeQuery(id+"F4.imprint","INTERSECT",VERTEX,{"derivedFrom":[subQ1,subQ0]});Q62=makeQuery(id+"F4.imprint","IMPRINT",FACE,{"disambiguationData":[TD([[makeQuery(id+"F4.imprint","IMPRINT",EDGE,{"disambiguationData":[TD([[subQ2,-1.0]])],"derivedFrom":subQ1}),1.0]])]});}
            var Q63;
            {var subQ0=sQuery(id+"F4.wireOp",EDGE,"E34.77.0");var subQ1=sQuery(id+"F4.wireOp",EDGE,"E29");var subQ2=makeQuery(id+"F4.imprint","INTERSECT",VERTEX,{"derivedFrom":[subQ1,subQ0]});Q63=makeQuery(id+"F4.imprint","IMPRINT",FACE,{"disambiguationData":[TD([[makeQuery(id+"F4.imprint","IMPRINT",EDGE,{"disambiguationData":[TD([[subQ2,-1.0]])],"derivedFrom":subQ1}),1.0]])]});}
            var Q64;
            {var subQ0=sQuery(id+"F4.wireOp",EDGE,"E34.78.0");var subQ1=sQuery(id+"F4.wireOp",EDGE,"E29");var subQ2=makeQuery(id+"F4.imprint","INTERSECT",VERTEX,{"derivedFrom":[subQ1,subQ0]});Q64=makeQuery(id+"F4.imprint","IMPRINT",FACE,{"disambiguationData":[TD([[makeQuery(id+"F4.imprint","IMPRINT",EDGE,{"disambiguationData":[TD([[subQ2,-1.0]])],"derivedFrom":subQ1}),1.0]])]});}
            var Q65;
            {var subQ0=sQuery(id+"F4.wireOp",EDGE,"E34.79.0");var subQ1=sQuery(id+"F4.wireOp",EDGE,"E29");var subQ2=makeQuery(id+"F4.imprint","INTERSECT",VERTEX,{"derivedFrom":[subQ1,subQ0]});Q65=makeQuery(id+"F4.imprint","IMPRINT",FACE,{"disambiguationData":[TD([[makeQuery(id+"F4.imprint","IMPRINT",EDGE,{"disambiguationData":[TD([[subQ2,-1.0]])],"derivedFrom":subQ1}),1.0]])]});}
            var Q66;
            {var subQ0=sQuery(id+"F4.wireOp",EDGE,"E34.80.0");var subQ1=sQuery(id+"F4.wireOp",EDGE,"E29");var subQ2=makeQuery(id+"F4.imprint","INTERSECT",VERTEX,{"derivedFrom":[subQ1,subQ0]});Q66=makeQuery(id+"F4.imprint","IMPRINT",FACE,{"disambiguationData":[TD([[makeQuery(id+"F4.imprint","IMPRINT",EDGE,{"disambiguationData":[TD([[subQ2,-1.0]])],"derivedFrom":subQ1}),1.0]])]});}
            var Q67;
            {var subQ0=sQuery(id+"F4.wireOp",EDGE,"E34.81.0");var subQ1=sQuery(id+"F4.wireOp",EDGE,"E29");var subQ2=makeQuery(id+"F4.imprint","INTERSECT",VERTEX,{"derivedFrom":[subQ1,subQ0]});Q67=makeQuery(id+"F4.imprint","IMPRINT",FACE,{"disambiguationData":[TD([[makeQuery(id+"F4.imprint","IMPRINT",EDGE,{"disambiguationData":[TD([[subQ2,-1.0]])],"derivedFrom":subQ1}),1.0]])]});}
            var Q68;
            {var subQ0=sQuery(id+"F4.wireOp",EDGE,"E34.82.0");var subQ1=sQuery(id+"F4.wireOp",EDGE,"E29");var subQ2=makeQuery(id+"F4.imprint","INTERSECT",VERTEX,{"derivedFrom":[subQ1,subQ0]});Q68=makeQuery(id+"F4.imprint","IMPRINT",FACE,{"disambiguationData":[TD([[makeQuery(id+"F4.imprint","IMPRINT",EDGE,{"disambiguationData":[TD([[subQ2,-1.0]])],"derivedFrom":subQ1}),1.0]])]});}
            var Q69;
            {var subQ0=sQuery(id+"F4.wireOp",EDGE,"E34.83.0");var subQ1=sQuery(id+"F4.wireOp",EDGE,"E29");var subQ2=makeQuery(id+"F4.imprint","INTERSECT",VERTEX,{"derivedFrom":[subQ1,subQ0]});Q69=makeQuery(id+"F4.imprint","IMPRINT",FACE,{"disambiguationData":[TD([[makeQuery(id+"F4.imprint","IMPRINT",EDGE,{"disambiguationData":[TD([[subQ2,-1.0]])],"derivedFrom":subQ1}),1.0]])]});}
            var Q70;
            {var subQ0=sQuery(id+"F4.wireOp",EDGE,"E34.84.0");var subQ1=sQuery(id+"F4.wireOp",EDGE,"E29");var subQ2=makeQuery(id+"F4.imprint","INTERSECT",VERTEX,{"derivedFrom":[subQ1,subQ0]});Q70=makeQuery(id+"F4.imprint","IMPRINT",FACE,{"disambiguationData":[TD([[makeQuery(id+"F4.imprint","IMPRINT",EDGE,{"disambiguationData":[TD([[subQ2,-1.0]])],"derivedFrom":subQ1}),1.0]])]});}
            var Q71;
            {var subQ0=sQuery(id+"F4.wireOp",EDGE,"E34.85.0");var subQ1=sQuery(id+"F4.wireOp",EDGE,"E29");var subQ2=makeQuery(id+"F4.imprint","INTERSECT",VERTEX,{"derivedFrom":[subQ1,subQ0]});Q71=makeQuery(id+"F4.imprint","IMPRINT",FACE,{"disambiguationData":[TD([[makeQuery(id+"F4.imprint","IMPRINT",EDGE,{"disambiguationData":[TD([[subQ2,-1.0]])],"derivedFrom":subQ1}),1.0]])]});}
            var Q72;
            {var subQ0=sQuery(id+"F4.wireOp",EDGE,"E34.86.0");var subQ1=sQuery(id+"F4.wireOp",EDGE,"E29");var subQ2=makeQuery(id+"F4.imprint","INTERSECT",VERTEX,{"derivedFrom":[subQ1,subQ0]});Q72=makeQuery(id+"F4.imprint","IMPRINT",FACE,{"disambiguationData":[TD([[makeQuery(id+"F4.imprint","IMPRINT",EDGE,{"disambiguationData":[TD([[subQ2,-1.0]])],"derivedFrom":subQ1}),1.0]])]});}
            var Q73;
            {var subQ0=sQuery(id+"F4.wireOp",EDGE,"E34.87.0");var subQ1=sQuery(id+"F4.wireOp",EDGE,"E29");var subQ2=makeQuery(id+"F4.imprint","INTERSECT",VERTEX,{"derivedFrom":[subQ1,subQ0]});Q73=makeQuery(id+"F4.imprint","IMPRINT",FACE,{"disambiguationData":[TD([[makeQuery(id+"F4.imprint","IMPRINT",EDGE,{"disambiguationData":[TD([[subQ2,-1.0]])],"derivedFrom":subQ1}),1.0]])]});}
            var Q74;
            {var subQ0=sQuery(id+"F4.wireOp",EDGE,"E34.88.0");var subQ1=sQuery(id+"F4.wireOp",EDGE,"E29");var subQ2=makeQuery(id+"F4.imprint","INTERSECT",VERTEX,{"derivedFrom":[subQ1,subQ0]});Q74=makeQuery(id+"F4.imprint","IMPRINT",FACE,{"disambiguationData":[TD([[makeQuery(id+"F4.imprint","IMPRINT",EDGE,{"disambiguationData":[TD([[subQ2,-1.0]])],"derivedFrom":subQ1}),1.0]])]});}
            var Q75;
            {var subQ0=sQuery(id+"F4.wireOp",EDGE,"E34.89.0");var subQ1=sQuery(id+"F4.wireOp",EDGE,"E29");var subQ2=makeQuery(id+"F4.imprint","INTERSECT",VERTEX,{"derivedFrom":[subQ1,subQ0]});Q75=makeQuery(id+"F4.imprint","IMPRINT",FACE,{"disambiguationData":[TD([[makeQuery(id+"F4.imprint","IMPRINT",EDGE,{"disambiguationData":[TD([[subQ2,-1.0]])],"derivedFrom":subQ1}),1.0]])]});}
            var Q76;
            {var subQ0=sQuery(id+"F4.wireOp",EDGE,"E34.90.0");var subQ1=sQuery(id+"F4.wireOp",EDGE,"E29");var subQ2=makeQuery(id+"F4.imprint","INTERSECT",VERTEX,{"derivedFrom":[subQ1,subQ0]});Q76=makeQuery(id+"F4.imprint","IMPRINT",FACE,{"disambiguationData":[TD([[makeQuery(id+"F4.imprint","IMPRINT",EDGE,{"disambiguationData":[TD([[subQ2,-1.0]])],"derivedFrom":subQ1}),1.0]])]});}
            var Q77;
            {var subQ0=sQuery(id+"F4.wireOp",EDGE,"E34.91.0");var subQ1=sQuery(id+"F4.wireOp",EDGE,"E29");var subQ2=makeQuery(id+"F4.imprint","INTERSECT",VERTEX,{"derivedFrom":[subQ1,subQ0]});Q77=makeQuery(id+"F4.imprint","IMPRINT",FACE,{"disambiguationData":[TD([[makeQuery(id+"F4.imprint","IMPRINT",EDGE,{"disambiguationData":[TD([[subQ2,-1.0]])],"derivedFrom":subQ1}),1.0]])]});}
            var Q78;
            {var subQ0=sQuery(id+"F4.wireOp",EDGE,"E34.92.0");var subQ1=sQuery(id+"F4.wireOp",EDGE,"E29");var subQ2=makeQuery(id+"F4.imprint","INTERSECT",VERTEX,{"derivedFrom":[subQ1,subQ0]});Q78=makeQuery(id+"F4.imprint","IMPRINT",FACE,{"disambiguationData":[TD([[makeQuery(id+"F4.imprint","IMPRINT",EDGE,{"disambiguationData":[TD([[subQ2,-1.0]])],"derivedFrom":subQ1}),1.0]])]});}
            var Q79;
            {var subQ0=sQuery(id+"F4.wireOp",EDGE,"E34.93.0");var subQ1=sQuery(id+"F4.wireOp",EDGE,"E29");var subQ2=makeQuery(id+"F4.imprint","INTERSECT",VERTEX,{"derivedFrom":[subQ1,subQ0]});Q79=makeQuery(id+"F4.imprint","IMPRINT",FACE,{"disambiguationData":[TD([[makeQuery(id+"F4.imprint","IMPRINT",EDGE,{"disambiguationData":[TD([[subQ2,-1.0]])],"derivedFrom":subQ1}),1.0]])]});}
            var Q80;
            {var subQ0=sQuery(id+"F4.wireOp",EDGE,"E34.94.0");var subQ1=sQuery(id+"F4.wireOp",EDGE,"E29");var subQ2=makeQuery(id+"F4.imprint","INTERSECT",VERTEX,{"derivedFrom":[subQ1,subQ0]});Q80=makeQuery(id+"F4.imprint","IMPRINT",FACE,{"disambiguationData":[TD([[makeQuery(id+"F4.imprint","IMPRINT",EDGE,{"disambiguationData":[TD([[subQ2,-1.0]])],"derivedFrom":subQ1}),1.0]])]});}
            var Q81;
            {var subQ0=sQuery(id+"F4.wireOp",EDGE,"E34.95.0");var subQ1=sQuery(id+"F4.wireOp",EDGE,"E29");var subQ2=makeQuery(id+"F4.imprint","INTERSECT",VERTEX,{"derivedFrom":[subQ1,subQ0]});Q81=makeQuery(id+"F4.imprint","IMPRINT",FACE,{"disambiguationData":[TD([[makeQuery(id+"F4.imprint","IMPRINT",EDGE,{"disambiguationData":[TD([[subQ2,-1.0]])],"derivedFrom":subQ1}),1.0]])]});}
            var Q82;
            {var subQ0=sQuery(id+"F4.wireOp",EDGE,"E34.96.0");var subQ1=sQuery(id+"F4.wireOp",EDGE,"E29");var subQ2=makeQuery(id+"F4.imprint","INTERSECT",VERTEX,{"derivedFrom":[subQ1,subQ0]});Q82=makeQuery(id+"F4.imprint","IMPRINT",FACE,{"disambiguationData":[TD([[makeQuery(id+"F4.imprint","IMPRINT",EDGE,{"disambiguationData":[TD([[subQ2,-1.0]])],"derivedFrom":subQ1}),1.0]])]});}
            var Q83;
            {var subQ0=sQuery(id+"F4.wireOp",EDGE,"E34.97.0");var subQ1=sQuery(id+"F4.wireOp",EDGE,"E29");var subQ2=makeQuery(id+"F4.imprint","INTERSECT",VERTEX,{"derivedFrom":[subQ1,subQ0]});Q83=makeQuery(id+"F4.imprint","IMPRINT",FACE,{"disambiguationData":[TD([[makeQuery(id+"F4.imprint","IMPRINT",EDGE,{"disambiguationData":[TD([[subQ2,-1.0]])],"derivedFrom":subQ1}),1.0]])]});}
            var Q84;
            {var subQ0=sQuery(id+"F4.wireOp",EDGE,"E34.98.0");var subQ1=sQuery(id+"F4.wireOp",EDGE,"E29");var subQ2=makeQuery(id+"F4.imprint","INTERSECT",VERTEX,{"derivedFrom":[subQ1,subQ0]});Q84=makeQuery(id+"F4.imprint","IMPRINT",FACE,{"disambiguationData":[TD([[makeQuery(id+"F4.imprint","IMPRINT",EDGE,{"disambiguationData":[TD([[subQ2,-1.0]])],"derivedFrom":subQ1}),1.0]])]});}
            var Q85;
            {var subQ0=sQuery(id+"F4.wireOp",EDGE,"E34.99.0");var subQ1=sQuery(id+"F4.wireOp",EDGE,"E29");var subQ2=makeQuery(id+"F4.imprint","INTERSECT",VERTEX,{"derivedFrom":[subQ1,subQ0]});Q85=makeQuery(id+"F4.imprint","IMPRINT",FACE,{"disambiguationData":[TD([[makeQuery(id+"F4.imprint","IMPRINT",EDGE,{"disambiguationData":[TD([[subQ2,-1.0]])],"derivedFrom":subQ1}),1.0]])]});}
            var Q86;
            {var subQ0=sQuery(id+"F4.wireOp",EDGE,"E34.100.0");var subQ1=sQuery(id+"F4.wireOp",EDGE,"E29");var subQ2=makeQuery(id+"F4.imprint","INTERSECT",VERTEX,{"derivedFrom":[subQ1,subQ0]});Q86=makeQuery(id+"F4.imprint","IMPRINT",FACE,{"disambiguationData":[TD([[makeQuery(id+"F4.imprint","IMPRINT",EDGE,{"disambiguationData":[TD([[subQ2,-1.0]])],"derivedFrom":subQ1}),1.0]])]});}
            var Q87;
            {var subQ0=sQuery(id+"F4.wireOp",EDGE,"E34.101.0");var subQ1=sQuery(id+"F4.wireOp",EDGE,"E29");var subQ2=makeQuery(id+"F4.imprint","INTERSECT",VERTEX,{"derivedFrom":[subQ1,subQ0]});Q87=makeQuery(id+"F4.imprint","IMPRINT",FACE,{"disambiguationData":[TD([[makeQuery(id+"F4.imprint","IMPRINT",EDGE,{"disambiguationData":[TD([[subQ2,-1.0]])],"derivedFrom":subQ1}),1.0]])]});}
            var Q88;
            {var subQ0=sQuery(id+"F4.wireOp",EDGE,"E34.102.0");var subQ1=sQuery(id+"F4.wireOp",EDGE,"E29");var subQ2=makeQuery(id+"F4.imprint","INTERSECT",VERTEX,{"derivedFrom":[subQ1,subQ0]});Q88=makeQuery(id+"F4.imprint","IMPRINT",FACE,{"disambiguationData":[TD([[makeQuery(id+"F4.imprint","IMPRINT",EDGE,{"disambiguationData":[TD([[subQ2,-1.0]])],"derivedFrom":subQ1}),1.0]])]});}
            var Q89;
            {var subQ1=sQuery(id+"F4.wireOp",EDGE,"E29");var subQ3=sQuery(id+"F4.wireOp",EDGE,"E34.103.0");var subQ5=makeQuery(id+"F4.imprint","INTERSECT",VERTEX,{"derivedFrom":[subQ1,subQ3]});Q89=makeQuery(id+"F4.imprint","IMPRINT",FACE,{"disambiguationData":[TD([[makeQuery(id+"F4.imprint","IMPRINT",EDGE,{"disambiguationData":[TD([[subQ5,-1.0]])],"derivedFrom":subQ1}),1.0]])]});}
            var Q90;
            {var subQ1=sQuery(id+"F4.wireOp",EDGE,"E29");var subQ3=sQuery(id+"F4.wireOp",EDGE,"E34.104.0");var subQ5=makeQuery(id+"F4.imprint","INTERSECT",VERTEX,{"derivedFrom":[subQ1,subQ3]});Q90=makeQuery(id+"F4.imprint","IMPRINT",FACE,{"disambiguationData":[TD([[makeQuery(id+"F4.imprint","IMPRINT",EDGE,{"disambiguationData":[TD([[subQ5,-1.0]])],"derivedFrom":subQ1}),1.0]])]});}
            var Q91;
            {var subQ0=sQuery(id+"F4.wireOp",EDGE,"E34.105.0");var subQ1=sQuery(id+"F4.wireOp",EDGE,"E29");var subQ2=makeQuery(id+"F4.imprint","INTERSECT",VERTEX,{"derivedFrom":[subQ1,subQ0]});Q91=makeQuery(id+"F4.imprint","IMPRINT",FACE,{"disambiguationData":[TD([[makeQuery(id+"F4.imprint","IMPRINT",EDGE,{"disambiguationData":[TD([[subQ2,-1.0]])],"derivedFrom":subQ1}),1.0]])]});}
            var Q92;
            {var subQ0=sQuery(id+"F4.wireOp",EDGE,"E34.106.0");var subQ1=sQuery(id+"F4.wireOp",EDGE,"E29");var subQ2=makeQuery(id+"F4.imprint","INTERSECT",VERTEX,{"derivedFrom":[subQ1,subQ0]});Q92=makeQuery(id+"F4.imprint","IMPRINT",FACE,{"disambiguationData":[TD([[makeQuery(id+"F4.imprint","IMPRINT",EDGE,{"disambiguationData":[TD([[subQ2,-1.0]])],"derivedFrom":subQ1}),1.0]])]});}
            var Q93;
            {var subQ0=sQuery(id+"F4.wireOp",EDGE,"E34.107.0");var subQ1=sQuery(id+"F4.wireOp",EDGE,"E29");var subQ2=makeQuery(id+"F4.imprint","INTERSECT",VERTEX,{"derivedFrom":[subQ1,subQ0]});Q93=makeQuery(id+"F4.imprint","IMPRINT",FACE,{"disambiguationData":[TD([[makeQuery(id+"F4.imprint","IMPRINT",EDGE,{"disambiguationData":[TD([[subQ2,-1.0]])],"derivedFrom":subQ1}),1.0]])]});}
            var Q94;
            {var subQ0=sQuery(id+"F4.wireOp",EDGE,"E34.108.0");var subQ1=sQuery(id+"F4.wireOp",EDGE,"E29");var subQ2=makeQuery(id+"F4.imprint","INTERSECT",VERTEX,{"derivedFrom":[subQ1,subQ0]});Q94=makeQuery(id+"F4.imprint","IMPRINT",FACE,{"disambiguationData":[TD([[makeQuery(id+"F4.imprint","IMPRINT",EDGE,{"disambiguationData":[TD([[subQ2,-1.0]])],"derivedFrom":subQ1}),1.0]])]});}
            var Q95;
            {var subQ0=sQuery(id+"F4.wireOp",EDGE,"E34.109.0");var subQ1=sQuery(id+"F4.wireOp",EDGE,"E29");var subQ2=makeQuery(id+"F4.imprint","INTERSECT",VERTEX,{"derivedFrom":[subQ1,subQ0]});Q95=makeQuery(id+"F4.imprint","IMPRINT",FACE,{"disambiguationData":[TD([[makeQuery(id+"F4.imprint","IMPRINT",EDGE,{"disambiguationData":[TD([[subQ2,-1.0]])],"derivedFrom":subQ1}),1.0]])]});}
            var Q96;
            {var subQ0=sQuery(id+"F4.wireOp",EDGE,"E34.110.0");var subQ1=sQuery(id+"F4.wireOp",EDGE,"E29");var subQ2=makeQuery(id+"F4.imprint","INTERSECT",VERTEX,{"derivedFrom":[subQ1,subQ0]});Q96=makeQuery(id+"F4.imprint","IMPRINT",FACE,{"disambiguationData":[TD([[makeQuery(id+"F4.imprint","IMPRINT",EDGE,{"disambiguationData":[TD([[subQ2,-1.0]])],"derivedFrom":subQ1}),1.0]])]});}
            var Q97;
            {var subQ0=sQuery(id+"F4.wireOp",EDGE,"E34.111.0");var subQ1=sQuery(id+"F4.wireOp",EDGE,"E29");var subQ2=makeQuery(id+"F4.imprint","INTERSECT",VERTEX,{"derivedFrom":[subQ1,subQ0]});Q97=makeQuery(id+"F4.imprint","IMPRINT",FACE,{"disambiguationData":[TD([[makeQuery(id+"F4.imprint","IMPRINT",EDGE,{"disambiguationData":[TD([[subQ2,-1.0]])],"derivedFrom":subQ1}),1.0]])]});}
            var Q98;
            {var subQ0=sQuery(id+"F4.wireOp",EDGE,"E34.112.0");var subQ1=sQuery(id+"F4.wireOp",EDGE,"E29");var subQ2=makeQuery(id+"F4.imprint","INTERSECT",VERTEX,{"derivedFrom":[subQ1,subQ0]});Q98=makeQuery(id+"F4.imprint","IMPRINT",FACE,{"disambiguationData":[TD([[makeQuery(id+"F4.imprint","IMPRINT",EDGE,{"disambiguationData":[TD([[subQ2,-1.0]])],"derivedFrom":subQ1}),1.0]])]});}
            var Q99;
            {var subQ0=sQuery(id+"F4.wireOp",EDGE,"E34.113.0");var subQ1=sQuery(id+"F4.wireOp",EDGE,"E29");var subQ2=makeQuery(id+"F4.imprint","INTERSECT",VERTEX,{"derivedFrom":[subQ1,subQ0]});Q99=makeQuery(id+"F4.imprint","IMPRINT",FACE,{"disambiguationData":[TD([[makeQuery(id+"F4.imprint","IMPRINT",EDGE,{"disambiguationData":[TD([[subQ2,-1.0]])],"derivedFrom":subQ1}),1.0]])]});}
            var Q100;
            {var subQ0=sQuery(id+"F4.wireOp",EDGE,"E34.114.0");var subQ1=sQuery(id+"F4.wireOp",EDGE,"E29");var subQ2=makeQuery(id+"F4.imprint","INTERSECT",VERTEX,{"derivedFrom":[subQ1,subQ0]});Q100=makeQuery(id+"F4.imprint","IMPRINT",FACE,{"disambiguationData":[TD([[makeQuery(id+"F4.imprint","IMPRINT",EDGE,{"disambiguationData":[TD([[subQ2,-1.0]])],"derivedFrom":subQ1}),1.0]])]});}
            var Q101;
            {var subQ0=sQuery(id+"F4.wireOp",EDGE,"E34.115.0");var subQ1=sQuery(id+"F4.wireOp",EDGE,"E29");var subQ2=makeQuery(id+"F4.imprint","INTERSECT",VERTEX,{"derivedFrom":[subQ1,subQ0]});Q101=makeQuery(id+"F4.imprint","IMPRINT",FACE,{"disambiguationData":[TD([[makeQuery(id+"F4.imprint","IMPRINT",EDGE,{"disambiguationData":[TD([[subQ2,-1.0]])],"derivedFrom":subQ1}),1.0]])]});}
            var Q102;
            {var subQ0=sQuery(id+"F4.wireOp",EDGE,"E34.116.0");var subQ1=sQuery(id+"F4.wireOp",EDGE,"E29");var subQ2=makeQuery(id+"F4.imprint","INTERSECT",VERTEX,{"derivedFrom":[subQ1,subQ0]});Q102=makeQuery(id+"F4.imprint","IMPRINT",FACE,{"disambiguationData":[TD([[makeQuery(id+"F4.imprint","IMPRINT",EDGE,{"disambiguationData":[TD([[subQ2,-1.0]])],"derivedFrom":subQ1}),1.0]])]});}
            var Q103;
            {var subQ0=sQuery(id+"F4.wireOp",EDGE,"E34.117.0");var subQ1=sQuery(id+"F4.wireOp",EDGE,"E29");var subQ2=makeQuery(id+"F4.imprint","INTERSECT",VERTEX,{"derivedFrom":[subQ1,subQ0]});Q103=makeQuery(id+"F4.imprint","IMPRINT",FACE,{"disambiguationData":[TD([[makeQuery(id+"F4.imprint","IMPRINT",EDGE,{"disambiguationData":[TD([[subQ2,-1.0]])],"derivedFrom":subQ1}),1.0]])]});}
            var Q104;
            {var subQ0=sQuery(id+"F4.wireOp",EDGE,"E34.118.0");var subQ1=sQuery(id+"F4.wireOp",EDGE,"E29");var subQ2=makeQuery(id+"F4.imprint","INTERSECT",VERTEX,{"derivedFrom":[subQ1,subQ0]});Q104=makeQuery(id+"F4.imprint","IMPRINT",FACE,{"disambiguationData":[TD([[makeQuery(id+"F4.imprint","IMPRINT",EDGE,{"disambiguationData":[TD([[subQ2,-1.0]])],"derivedFrom":subQ1}),1.0]])]});}
            var Q105;
            {var subQ0=sQuery(id+"F4.wireOp",EDGE,"E34.119.0");var subQ1=sQuery(id+"F4.wireOp",EDGE,"E29");var subQ2=makeQuery(id+"F4.imprint","INTERSECT",VERTEX,{"derivedFrom":[subQ1,subQ0]});Q105=makeQuery(id+"F4.imprint","IMPRINT",FACE,{"disambiguationData":[TD([[makeQuery(id+"F4.imprint","IMPRINT",EDGE,{"disambiguationData":[TD([[subQ2,-1.0]])],"derivedFrom":subQ1}),1.0]])]});}
            var Q106;
            {var subQ1=sQuery(id+"F4.wireOp",EDGE,"E32");var subQ3=sQuery(id+"F4.wireOp",EDGE,"E29");var subQ5=makeQuery(id+"F4.imprint","INTERSECT",VERTEX,{"derivedFrom":[subQ3,subQ1]});Q106=makeQuery(id+"F4.imprint","IMPRINT",FACE,{"disambiguationData":[TD([[makeQuery(id+"F4.imprint","IMPRINT",EDGE,{"disambiguationData":[TD([[subQ5,-1.0]])],"derivedFrom":subQ3}),1.0]])]});}
            extrude(context, id + "F5", {"entities" : qUnion([Q0, Q1, Q2, Q3, Q4, Q5, Q6, Q7, Q8, Q9, Q10, Q11, Q12, Q13, Q14, Q15, Q16, Q17, Q18, Q19, Q20, Q21, Q22, Q23, Q24, Q25, Q26, Q27, Q28, Q29, Q30, Q31, Q32, Q33, Q34, Q35, Q36, Q37, Q38, Q39, Q40, Q41, Q42, Q43, Q44, Q45, Q46, Q47, Q48, Q49, Q50, Q51, Q52, Q53, Q54, Q55, Q56, Q57, Q58, Q59, Q60, Q61, Q62, Q63, Q64, Q65, Q66, Q67, Q68, Q69, Q70, Q71, Q72, Q73, Q74, Q75, Q76, Q77, Q78, Q79, Q80, Q81, Q82, Q83, Q84, Q85, Q86, Q87, Q88, Q89, Q90, Q91, Q92, Q93, Q94, Q95, Q96, Q97, Q98, Q99, Q100, Q101, Q102, Q103, Q104, Q105, Q106]), "operationType" : NewBodyOperationType.REMOVE, "endBound" : BoundingType.THROUGH_ALL, "depth" : 25 * mm});
        }
    });
